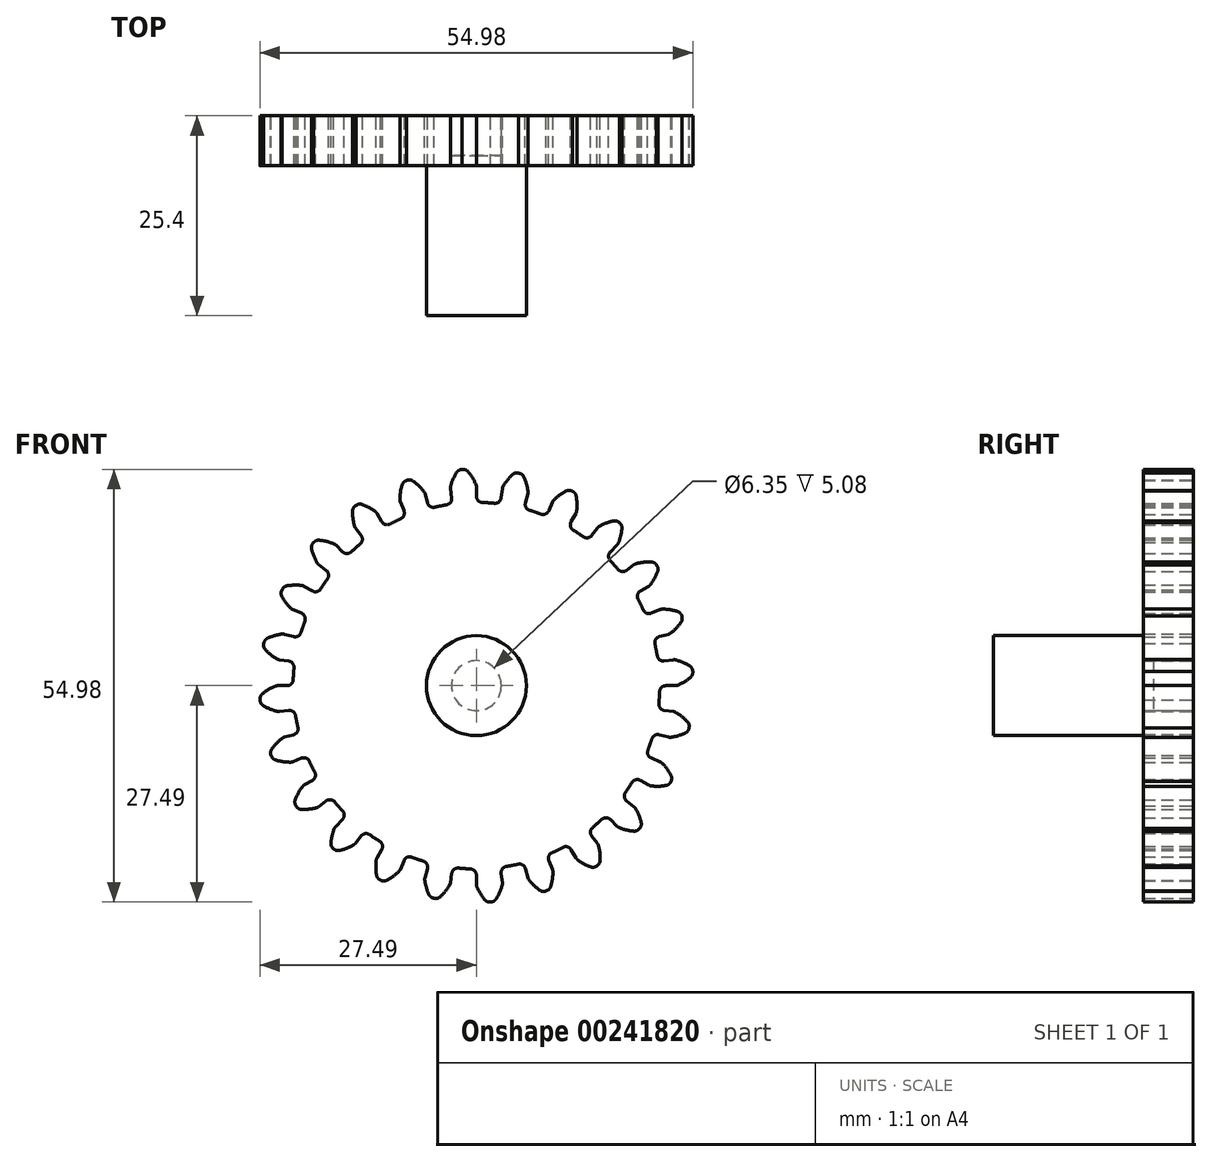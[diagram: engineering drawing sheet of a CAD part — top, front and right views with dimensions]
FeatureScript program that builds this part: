
annotation { "Feature Type Name" : "Feature", "Feature Type Description" : "" }
export const myFeature = defineFeature(function(context is Context, id is Id, definition is map)
    precondition{}
    {
        {
            var Q0;
            Q0=qCreatedBy(makeId("Front.planeOp"),FACE);
            var sketch = newSketch(context, id + "F0", { "sketchPlane" : qUnion([Q0])});
            skArc(sketch, "E0", {"start": v(-3.8, 22.97) * mm, "mid": v(-4.54, 22.84) * mm, "end": v(-5.28, 22.68) * mm});
            skArc(sketch, "E1.trimOffspring", {"start": v(-0.06, 25.55) * mm, "mid": v(-0.5, 26.41) * mm, "end": v(-1.06, 27.2) * mm});
            skLineSegment(sketch, "E2", {"start": v(0, 25.25) * mm, "end": v(0, 24.06) * mm});
            skLineSegment(sketch, "E3", {"start": v(-1.67, 27.49) * mm, "end": v(-1.8, 27.49) * mm});
            skLineSegment(sketch, "E4.MirrorCS", {"start": v(-1.93, 27.47) * mm, "end": v(-1.8, 27.49) * mm});
            skArc(sketch, "E5.MirrorCS", {"start": v(-3.28, 25.34) * mm, "mid": v(-2.95, 26.25) * mm, "end": v(-2.5, 27.1) * mm});
            skLineSegment(sketch, "E6.MirrorCS", {"start": v(-3.3, 25.03) * mm, "end": v(-3.14, 23.86) * mm});
            skPoint(sketch, "E7.visualSharp", {"position": v(-3.04, 23.08) * mm});
            skArc(sketch, "E8.filletArc", {"start": v(-3.8, 22.97) * mm, "mid": v(-3.3, 23.28) * mm, "end": v(-3.14, 23.86) * mm});
            skPoint(sketch, "E9.visualSharp", {"position": v(-3.32, 25.18) * mm});
            skArc(sketch, "E9.filletArc", {"start": v(-3.28, 25.34) * mm, "mid": v(-3.3, 25.19) * mm, "end": v(-3.3, 25.03) * mm});
            skPoint(sketch, "E10.visualSharp", {"position": v(-2.28, 27.42) * mm});
            skArc(sketch, "E10.filletArc", {"start": v(-1.93, 27.47) * mm, "mid": v(-2.25, 27.35) * mm, "end": v(-2.5, 27.1) * mm});
            skPoint(sketch, "E11.visualSharp", {"position": v(0, 25.4) * mm});
            skArc(sketch, "E11.filletArc", {"start": v(0, 25.25) * mm, "mid": v(-0.02, 25.4) * mm, "end": v(-0.06, 25.55) * mm});
            skPoint(sketch, "E12.visualSharp", {"position": v(0, 23.28) * mm});
            skArc(sketch, "E12.filletArc", {"start": v(0, 24.06) * mm, "mid": v(0.22, 23.51) * mm, "end": v(0.77, 23.27) * mm});
            skPoint(sketch, "E13.visualSharp", {"position": v(-1.31, 27.49) * mm});
            skArc(sketch, "E13.filletArc", {"start": v(-1.06, 27.2) * mm, "mid": v(-1.33, 27.41) * mm, "end": v(-1.67, 27.49) * mm});
            skArc(sketch, "E14.1.0", {"start": v(-9.61, 21.2) * mm, "mid": v(-9.2, 21.64) * mm, "end": v(-9.2, 22.23) * mm});
            skLineSegment(sketch, "E14.1.1", {"start": v(-9.66, 23.33) * mm, "end": v(-9.2, 22.23) * mm});
            skArc(sketch, "E14.1.2", {"start": v(-9.72, 23.63) * mm, "mid": v(-9.7, 23.47) * mm, "end": v(-9.66, 23.33) * mm});
            skArc(sketch, "E14.1.3", {"start": v(-9.72, 23.63) * mm, "mid": v(-9.65, 24.6) * mm, "end": v(-9.43, 25.54) * mm});
            skArc(sketch, "E14.1.4", {"start": v(-8.98, 26.03) * mm, "mid": v(-9.26, 25.83) * mm, "end": v(-9.43, 25.54) * mm});
            skLineSegment(sketch, "E14.1.5", {"start": v(-8.98, 26.03) * mm, "end": v(-8.85, 26.08) * mm});
            skLineSegment(sketch, "E14.1.6", {"start": v(-8.73, 26.12) * mm, "end": v(-8.85, 26.08) * mm});
            skArc(sketch, "E14.1.7", {"start": v(-8.07, 26) * mm, "mid": v(-8.38, 26.13) * mm, "end": v(-8.73, 26.12) * mm});
            skArc(sketch, "E14.1.8", {"start": v(-6.67, 24.67) * mm, "mid": v(-7.32, 25.39) * mm, "end": v(-8.07, 26) * mm});
            skArc(sketch, "E14.1.9", {"start": v(-6.53, 24.39) * mm, "mid": v(-6.59, 24.53) * mm, "end": v(-6.67, 24.67) * mm});
            skLineSegment(sketch, "E14.1.10", {"start": v(-6.53, 24.39) * mm, "end": v(-6.23, 23.24) * mm});
            skArc(sketch, "E14.1.11", {"start": v(-6.23, 23.24) * mm, "mid": v(-5.87, 22.77) * mm, "end": v(-5.28, 22.68) * mm});
            skArc(sketch, "E14.2.0", {"start": v(-14.78, 18) * mm, "mid": v(-14.5, 18.52) * mm, "end": v(-14.65, 19.1) * mm});
            skLineSegment(sketch, "E14.2.1", {"start": v(-15.37, 20.03) * mm, "end": v(-14.65, 19.1) * mm});
            skArc(sketch, "E14.2.2", {"start": v(-15.5, 20.3) * mm, "mid": v(-15.45, 20.16) * mm, "end": v(-15.37, 20.03) * mm});
            skArc(sketch, "E14.2.3", {"start": v(-15.5, 20.3) * mm, "mid": v(-15.69, 21.26) * mm, "end": v(-15.72, 22.23) * mm});
            skArc(sketch, "E14.2.4", {"start": v(-15.4, 22.82) * mm, "mid": v(-15.63, 22.56) * mm, "end": v(-15.72, 22.23) * mm});
            skLineSegment(sketch, "E14.2.5", {"start": v(-15.4, 22.82) * mm, "end": v(-15.3, 22.9) * mm});
            skLineSegment(sketch, "E14.2.6", {"start": v(-15.19, 22.97) * mm, "end": v(-15.3, 22.9) * mm});
            skArc(sketch, "E14.2.7", {"start": v(-14.52, 23.03) * mm, "mid": v(-14.86, 23.07) * mm, "end": v(-15.19, 22.97) * mm});
            skArc(sketch, "E14.2.8", {"start": v(-12.83, 22.1) * mm, "mid": v(-13.64, 22.63) * mm, "end": v(-14.52, 23.03) * mm});
            skArc(sketch, "E14.2.9", {"start": v(-12.62, 21.87) * mm, "mid": v(-12.71, 22) * mm, "end": v(-12.83, 22.1) * mm});
            skLineSegment(sketch, "E14.2.10", {"start": v(-12.62, 21.87) * mm, "end": v(-12.03, 20.84) * mm});
            skArc(sketch, "E14.2.11", {"start": v(-12.03, 20.84) * mm, "mid": v(-11.56, 20.47) * mm, "end": v(-10.97, 20.54) * mm});
            skArc(sketch, "E15.2.3.0", {"start": v(-18.93, 13.56) * mm, "mid": v(-18.79, 14.14) * mm, "end": v(-19.1, 14.65) * mm});
            skLineSegment(sketch, "E15.4.3.0", {"start": v(-20.03, 15.37) * mm, "end": v(-19.1, 14.65) * mm});
            skArc(sketch, "E15.7.3.0", {"start": v(-20.23, 15.6) * mm, "mid": v(-20.14, 15.48) * mm, "end": v(-20.03, 15.37) * mm});
            skArc(sketch, "E15.11.3.0", {"start": v(-20.23, 15.6) * mm, "mid": v(-20.65, 16.48) * mm, "end": v(-20.93, 17.4) * mm});
            skArc(sketch, "E15.15.3.0", {"start": v(-20.79, 18.06) * mm, "mid": v(-20.93, 17.75) * mm, "end": v(-20.93, 17.4) * mm});
            skLineSegment(sketch, "E15.19.3.0", {"start": v(-20.79, 18.06) * mm, "end": v(-20.7, 18.16) * mm});
            skLineSegment(sketch, "E15.22.3.0", {"start": v(-20.62, 18.25) * mm, "end": v(-20.7, 18.16) * mm});
            skArc(sketch, "E15.25.3.0", {"start": v(-19.99, 18.48) * mm, "mid": v(-20.33, 18.44) * mm, "end": v(-20.62, 18.25) * mm});
            skArc(sketch, "E15.29.3.0", {"start": v(-18.11, 18.02) * mm, "mid": v(-19.03, 18.33) * mm, "end": v(-19.99, 18.48) * mm});
            skArc(sketch, "E15.33.3.0", {"start": v(-17.85, 17.85) * mm, "mid": v(-17.97, 17.95) * mm, "end": v(-18.11, 18.02) * mm});
            skLineSegment(sketch, "E15.37.3.0", {"start": v(-17.85, 17.85) * mm, "end": v(-17.02, 17.02) * mm});
            skArc(sketch, "E15.40.3.0", {"start": v(-17.02, 17.02) * mm, "mid": v(-16.47, 16.78) * mm, "end": v(-15.91, 17) * mm});
            skArc(sketch, "E15.2.4.0", {"start": v(-21.8, 8.2) * mm, "mid": v(-21.8, 8.8) * mm, "end": v(-22.23, 9.2) * mm});
            skLineSegment(sketch, "E15.4.4.0", {"start": v(-23.33, 9.66) * mm, "end": v(-22.23, 9.2) * mm});
            skArc(sketch, "E15.7.4.0", {"start": v(-23.58, 9.83) * mm, "mid": v(-23.46, 9.74) * mm, "end": v(-23.33, 9.66) * mm});
            skArc(sketch, "E15.11.4.0", {"start": v(-23.58, 9.83) * mm, "mid": v(-24.21, 10.57) * mm, "end": v(-24.72, 11.4) * mm});
            skArc(sketch, "E15.15.4.0", {"start": v(-24.75, 12.06) * mm, "mid": v(-24.81, 11.72) * mm, "end": v(-24.72, 11.4) * mm});
            skLineSegment(sketch, "E15.19.4.0", {"start": v(-24.75, 12.06) * mm, "end": v(-24.7, 12.18) * mm});
            skLineSegment(sketch, "E15.22.4.0", {"start": v(-24.64, 12.3) * mm, "end": v(-24.7, 12.18) * mm});
            skArc(sketch, "E15.25.4.0", {"start": v(-24.09, 12.68) * mm, "mid": v(-24.4, 12.55) * mm, "end": v(-24.64, 12.3) * mm});
            skArc(sketch, "E15.29.4.0", {"start": v(-22.16, 12.72) * mm, "mid": v(-23.12, 12.78) * mm, "end": v(-24.09, 12.68) * mm});
            skArc(sketch, "E15.33.4.0", {"start": v(-21.87, 12.62) * mm, "mid": v(-22, 12.69) * mm, "end": v(-22.16, 12.72) * mm});
            skLineSegment(sketch, "E15.37.4.0", {"start": v(-21.87, 12.62) * mm, "end": v(-20.84, 12.03) * mm});
            skArc(sketch, "E15.40.4.0", {"start": v(-20.84, 12.03) * mm, "mid": v(-20.25, 11.95) * mm, "end": v(-19.77, 12.3) * mm});
            skArc(sketch, "E15.2.5.0", {"start": v(-23.17, 2.28) * mm, "mid": v(-23.34, 2.85) * mm, "end": v(-23.86, 3.14) * mm});
            skLineSegment(sketch, "E15.4.5.0", {"start": v(-25.03, 3.3) * mm, "end": v(-23.86, 3.14) * mm});
            skArc(sketch, "E15.7.5.0", {"start": v(-25.32, 3.4) * mm, "mid": v(-25.18, 3.33) * mm, "end": v(-25.03, 3.3) * mm});
            skArc(sketch, "E15.11.5.0", {"start": v(-25.32, 3.4) * mm, "mid": v(-26.12, 3.94) * mm, "end": v(-26.83, 4.6) * mm});
            skArc(sketch, "E15.15.5.0", {"start": v(-27.03, 5.24) * mm, "mid": v(-27, 4.9) * mm, "end": v(-26.83, 4.6) * mm});
            skLineSegment(sketch, "E15.19.5.0", {"start": v(-27.03, 5.24) * mm, "end": v(-27.01, 5.37) * mm});
            skLineSegment(sketch, "E15.22.5.0", {"start": v(-26.98, 5.5) * mm, "end": v(-27.01, 5.37) * mm});
            skArc(sketch, "E15.25.5.0", {"start": v(-26.55, 6.01) * mm, "mid": v(-26.82, 5.8) * mm, "end": v(-26.98, 5.5) * mm});
            skArc(sketch, "E15.29.5.0", {"start": v(-24.7, 6.55) * mm, "mid": v(-25.64, 6.36) * mm, "end": v(-26.55, 6.01) * mm});
            skArc(sketch, "E15.33.5.0", {"start": v(-24.39, 6.53) * mm, "mid": v(-24.54, 6.56) * mm, "end": v(-24.7, 6.55) * mm});
            skLineSegment(sketch, "E15.37.5.0", {"start": v(-24.39, 6.53) * mm, "end": v(-23.24, 6.23) * mm});
            skArc(sketch, "E15.40.5.0", {"start": v(-23.24, 6.23) * mm, "mid": v(-22.65, 6.3) * mm, "end": v(-22.28, 6.76) * mm});
            skArc(sketch, "E15.2.6.0", {"start": v(-22.97, -3.8) * mm, "mid": v(-23.28, -3.3) * mm, "end": v(-23.86, -3.14) * mm});
            skLineSegment(sketch, "E15.4.6.0", {"start": v(-25.03, -3.3) * mm, "end": v(-23.86, -3.14) * mm});
            skArc(sketch, "E15.7.6.0", {"start": v(-25.34, -3.28) * mm, "mid": v(-25.19, -3.3) * mm, "end": v(-25.03, -3.3) * mm});
            skArc(sketch, "E15.11.6.0", {"start": v(-25.34, -3.28) * mm, "mid": v(-26.25, -2.95) * mm, "end": v(-27.1, -2.5) * mm});
            skArc(sketch, "E15.15.6.0", {"start": v(-27.47, -1.93) * mm, "mid": v(-27.35, -2.25) * mm, "end": v(-27.1, -2.5) * mm});
            skLineSegment(sketch, "E15.19.6.0", {"start": v(-27.47, -1.93) * mm, "end": v(-27.49, -1.8) * mm});
            skLineSegment(sketch, "E15.22.6.0", {"start": v(-27.49, -1.67) * mm, "end": v(-27.49, -1.8) * mm});
            skArc(sketch, "E15.25.6.0", {"start": v(-27.2, -1.06) * mm, "mid": v(-27.41, -1.33) * mm, "end": v(-27.49, -1.67) * mm});
            skArc(sketch, "E15.29.6.0", {"start": v(-25.55, -0.06) * mm, "mid": v(-26.41, -0.5) * mm, "end": v(-27.2, -1.06) * mm});
            skArc(sketch, "E15.33.6.0", {"start": v(-25.25, 0) * mm, "mid": v(-25.4, -0.02) * mm, "end": v(-25.55, -0.06) * mm});
            skLineSegment(sketch, "E15.37.6.0", {"start": v(-25.25, 0) * mm, "end": v(-24.06, 0) * mm});
            skArc(sketch, "E15.40.6.0", {"start": v(-24.06, 0) * mm, "mid": v(-23.51, 0.22) * mm, "end": v(-23.27, 0.77) * mm});
            skArc(sketch, "E15.2.7.0", {"start": v(-21.2, -9.61) * mm, "mid": v(-21.64, -9.2) * mm, "end": v(-22.23, -9.2) * mm});
            skLineSegment(sketch, "E15.4.7.0", {"start": v(-23.33, -9.66) * mm, "end": v(-22.23, -9.2) * mm});
            skArc(sketch, "E15.7.7.0", {"start": v(-23.63, -9.72) * mm, "mid": v(-23.47, -9.7) * mm, "end": v(-23.33, -9.66) * mm});
            skArc(sketch, "E15.11.7.0", {"start": v(-23.63, -9.72) * mm, "mid": v(-24.6, -9.65) * mm, "end": v(-25.54, -9.43) * mm});
            skArc(sketch, "E15.15.7.0", {"start": v(-26.03, -8.98) * mm, "mid": v(-25.83, -9.26) * mm, "end": v(-25.54, -9.43) * mm});
            skLineSegment(sketch, "E15.19.7.0", {"start": v(-26.03, -8.98) * mm, "end": v(-26.08, -8.85) * mm});
            skLineSegment(sketch, "E15.22.7.0", {"start": v(-26.12, -8.73) * mm, "end": v(-26.08, -8.85) * mm});
            skArc(sketch, "E15.25.7.0", {"start": v(-26, -8.07) * mm, "mid": v(-26.13, -8.38) * mm, "end": v(-26.12, -8.73) * mm});
            skArc(sketch, "E15.29.7.0", {"start": v(-24.67, -6.67) * mm, "mid": v(-25.39, -7.32) * mm, "end": v(-26, -8.07) * mm});
            skArc(sketch, "E15.33.7.0", {"start": v(-24.39, -6.53) * mm, "mid": v(-24.53, -6.59) * mm, "end": v(-24.67, -6.67) * mm});
            skLineSegment(sketch, "E15.37.7.0", {"start": v(-24.39, -6.53) * mm, "end": v(-23.24, -6.23) * mm});
            skArc(sketch, "E15.40.7.0", {"start": v(-23.24, -6.23) * mm, "mid": v(-22.77, -5.87) * mm, "end": v(-22.68, -5.28) * mm});
            skArc(sketch, "E15.2.8.0", {"start": v(-18, -14.78) * mm, "mid": v(-18.52, -14.5) * mm, "end": v(-19.1, -14.65) * mm});
            skLineSegment(sketch, "E15.4.8.0", {"start": v(-20.03, -15.37) * mm, "end": v(-19.1, -14.65) * mm});
            skArc(sketch, "E15.7.8.0", {"start": v(-20.3, -15.5) * mm, "mid": v(-20.16, -15.45) * mm, "end": v(-20.03, -15.37) * mm});
            skArc(sketch, "E15.11.8.0", {"start": v(-20.3, -15.5) * mm, "mid": v(-21.26, -15.69) * mm, "end": v(-22.23, -15.72) * mm});
            skArc(sketch, "E15.15.8.0", {"start": v(-22.82, -15.4) * mm, "mid": v(-22.56, -15.63) * mm, "end": v(-22.23, -15.72) * mm});
            skLineSegment(sketch, "E15.19.8.0", {"start": v(-22.82, -15.4) * mm, "end": v(-22.9, -15.3) * mm});
            skLineSegment(sketch, "E15.22.8.0", {"start": v(-22.97, -15.19) * mm, "end": v(-22.9, -15.3) * mm});
            skArc(sketch, "E15.25.8.0", {"start": v(-23.03, -14.52) * mm, "mid": v(-23.07, -14.86) * mm, "end": v(-22.97, -15.19) * mm});
            skArc(sketch, "E15.29.8.0", {"start": v(-22.1, -12.83) * mm, "mid": v(-22.63, -13.64) * mm, "end": v(-23.03, -14.52) * mm});
            skArc(sketch, "E15.33.8.0", {"start": v(-21.87, -12.62) * mm, "mid": v(-22, -12.71) * mm, "end": v(-22.1, -12.83) * mm});
            skLineSegment(sketch, "E15.37.8.0", {"start": v(-21.87, -12.62) * mm, "end": v(-20.84, -12.03) * mm});
            skArc(sketch, "E15.40.8.0", {"start": v(-20.84, -12.03) * mm, "mid": v(-20.47, -11.56) * mm, "end": v(-20.54, -10.97) * mm});
            skArc(sketch, "E15.2.9.0", {"start": v(-13.56, -18.93) * mm, "mid": v(-14.14, -18.79) * mm, "end": v(-14.65, -19.1) * mm});
            skLineSegment(sketch, "E15.4.9.0", {"start": v(-15.37, -20.03) * mm, "end": v(-14.65, -19.1) * mm});
            skArc(sketch, "E15.7.9.0", {"start": v(-15.6, -20.23) * mm, "mid": v(-15.48, -20.14) * mm, "end": v(-15.37, -20.03) * mm});
            skArc(sketch, "E15.11.9.0", {"start": v(-15.6, -20.23) * mm, "mid": v(-16.48, -20.65) * mm, "end": v(-17.4, -20.93) * mm});
            skArc(sketch, "E15.15.9.0", {"start": v(-18.06, -20.79) * mm, "mid": v(-17.75, -20.93) * mm, "end": v(-17.4, -20.93) * mm});
            skLineSegment(sketch, "E15.19.9.0", {"start": v(-18.06, -20.79) * mm, "end": v(-18.16, -20.7) * mm});
            skLineSegment(sketch, "E15.22.9.0", {"start": v(-18.25, -20.62) * mm, "end": v(-18.16, -20.7) * mm});
            skArc(sketch, "E15.25.9.0", {"start": v(-18.48, -19.99) * mm, "mid": v(-18.44, -20.33) * mm, "end": v(-18.25, -20.62) * mm});
            skArc(sketch, "E15.29.9.0", {"start": v(-18.02, -18.11) * mm, "mid": v(-18.33, -19.03) * mm, "end": v(-18.48, -19.99) * mm});
            skArc(sketch, "E15.33.9.0", {"start": v(-17.85, -17.85) * mm, "mid": v(-17.95, -17.97) * mm, "end": v(-18.02, -18.11) * mm});
            skLineSegment(sketch, "E15.37.9.0", {"start": v(-17.85, -17.85) * mm, "end": v(-17.02, -17.02) * mm});
            skArc(sketch, "E15.40.9.0", {"start": v(-17.02, -17.02) * mm, "mid": v(-16.78, -16.47) * mm, "end": v(-17, -15.91) * mm});
            skArc(sketch, "E15.2.10.0", {"start": v(-8.2, -21.8) * mm, "mid": v(-8.8, -21.8) * mm, "end": v(-9.2, -22.23) * mm});
            skLineSegment(sketch, "E15.4.10.0", {"start": v(-9.66, -23.33) * mm, "end": v(-9.2, -22.23) * mm});
            skArc(sketch, "E15.7.10.0", {"start": v(-9.83, -23.58) * mm, "mid": v(-9.74, -23.46) * mm, "end": v(-9.66, -23.33) * mm});
            skArc(sketch, "E15.11.10.0", {"start": v(-9.83, -23.58) * mm, "mid": v(-10.57, -24.21) * mm, "end": v(-11.4, -24.72) * mm});
            skArc(sketch, "E15.15.10.0", {"start": v(-12.06, -24.75) * mm, "mid": v(-11.72, -24.81) * mm, "end": v(-11.4, -24.72) * mm});
            skLineSegment(sketch, "E15.19.10.0", {"start": v(-12.06, -24.75) * mm, "end": v(-12.18, -24.7) * mm});
            skLineSegment(sketch, "E15.22.10.0", {"start": v(-12.3, -24.64) * mm, "end": v(-12.18, -24.7) * mm});
            skArc(sketch, "E15.25.10.0", {"start": v(-12.68, -24.09) * mm, "mid": v(-12.55, -24.4) * mm, "end": v(-12.3, -24.64) * mm});
            skArc(sketch, "E15.29.10.0", {"start": v(-12.72, -22.16) * mm, "mid": v(-12.78, -23.12) * mm, "end": v(-12.68, -24.09) * mm});
            skArc(sketch, "E15.33.10.0", {"start": v(-12.62, -21.87) * mm, "mid": v(-12.69, -22) * mm, "end": v(-12.72, -22.16) * mm});
            skLineSegment(sketch, "E15.37.10.0", {"start": v(-12.62, -21.87) * mm, "end": v(-12.03, -20.84) * mm});
            skArc(sketch, "E15.40.10.0", {"start": v(-12.03, -20.84) * mm, "mid": v(-11.95, -20.25) * mm, "end": v(-12.3, -19.77) * mm});
            skArc(sketch, "E15.2.11.0", {"start": v(-2.28, -23.17) * mm, "mid": v(-2.85, -23.34) * mm, "end": v(-3.14, -23.86) * mm});
            skLineSegment(sketch, "E15.4.11.0", {"start": v(-3.3, -25.03) * mm, "end": v(-3.14, -23.86) * mm});
            skArc(sketch, "E15.7.11.0", {"start": v(-3.4, -25.32) * mm, "mid": v(-3.33, -25.18) * mm, "end": v(-3.3, -25.03) * mm});
            skArc(sketch, "E15.11.11.0", {"start": v(-3.4, -25.32) * mm, "mid": v(-3.94, -26.12) * mm, "end": v(-4.6, -26.83) * mm});
            skArc(sketch, "E15.15.11.0", {"start": v(-5.24, -27.03) * mm, "mid": v(-4.9, -27) * mm, "end": v(-4.6, -26.83) * mm});
            skLineSegment(sketch, "E15.19.11.0", {"start": v(-5.24, -27.03) * mm, "end": v(-5.37, -27.01) * mm});
            skLineSegment(sketch, "E15.22.11.0", {"start": v(-5.5, -26.98) * mm, "end": v(-5.37, -27.01) * mm});
            skArc(sketch, "E15.25.11.0", {"start": v(-6.01, -26.55) * mm, "mid": v(-5.8, -26.82) * mm, "end": v(-5.5, -26.98) * mm});
            skArc(sketch, "E15.29.11.0", {"start": v(-6.55, -24.7) * mm, "mid": v(-6.36, -25.64) * mm, "end": v(-6.01, -26.55) * mm});
            skArc(sketch, "E15.33.11.0", {"start": v(-6.53, -24.39) * mm, "mid": v(-6.56, -24.54) * mm, "end": v(-6.55, -24.7) * mm});
            skLineSegment(sketch, "E15.37.11.0", {"start": v(-6.53, -24.39) * mm, "end": v(-6.23, -23.24) * mm});
            skArc(sketch, "E15.40.11.0", {"start": v(-6.23, -23.24) * mm, "mid": v(-6.3, -22.65) * mm, "end": v(-6.76, -22.28) * mm});
            skArc(sketch, "E15.2.12.0", {"start": v(3.8, -22.97) * mm, "mid": v(3.3, -23.28) * mm, "end": v(3.14, -23.86) * mm});
            skLineSegment(sketch, "E15.4.12.0", {"start": v(3.3, -25.03) * mm, "end": v(3.14, -23.86) * mm});
            skArc(sketch, "E15.7.12.0", {"start": v(3.28, -25.34) * mm, "mid": v(3.3, -25.19) * mm, "end": v(3.3, -25.03) * mm});
            skArc(sketch, "E15.11.12.0", {"start": v(3.28, -25.34) * mm, "mid": v(2.95, -26.25) * mm, "end": v(2.5, -27.1) * mm});
            skArc(sketch, "E15.15.12.0", {"start": v(1.93, -27.47) * mm, "mid": v(2.25, -27.35) * mm, "end": v(2.5, -27.1) * mm});
            skLineSegment(sketch, "E15.19.12.0", {"start": v(1.93, -27.47) * mm, "end": v(1.8, -27.49) * mm});
            skLineSegment(sketch, "E15.22.12.0", {"start": v(1.67, -27.49) * mm, "end": v(1.8, -27.49) * mm});
            skArc(sketch, "E15.25.12.0", {"start": v(1.06, -27.2) * mm, "mid": v(1.33, -27.41) * mm, "end": v(1.67, -27.49) * mm});
            skArc(sketch, "E15.29.12.0", {"start": v(0.06, -25.55) * mm, "mid": v(0.5, -26.41) * mm, "end": v(1.06, -27.2) * mm});
            skArc(sketch, "E15.33.12.0", {"start": v(0, -25.25) * mm, "mid": v(0.02, -25.4) * mm, "end": v(0.06, -25.55) * mm});
            skLineSegment(sketch, "E15.37.12.0", {"start": v(0, -25.25) * mm, "end": v(0, -24.06) * mm});
            skArc(sketch, "E15.40.12.0", {"start": v(0, -24.06) * mm, "mid": v(-0.22, -23.51) * mm, "end": v(-0.77, -23.27) * mm});
            skArc(sketch, "E15.2.13.0", {"start": v(9.61, -21.2) * mm, "mid": v(9.2, -21.64) * mm, "end": v(9.2, -22.23) * mm});
            skLineSegment(sketch, "E15.4.13.0", {"start": v(9.66, -23.33) * mm, "end": v(9.2, -22.23) * mm});
            skArc(sketch, "E15.7.13.0", {"start": v(9.72, -23.63) * mm, "mid": v(9.7, -23.47) * mm, "end": v(9.66, -23.33) * mm});
            skArc(sketch, "E15.11.13.0", {"start": v(9.72, -23.63) * mm, "mid": v(9.65, -24.6) * mm, "end": v(9.43, -25.54) * mm});
            skArc(sketch, "E15.15.13.0", {"start": v(8.98, -26.03) * mm, "mid": v(9.26, -25.83) * mm, "end": v(9.43, -25.54) * mm});
            skLineSegment(sketch, "E15.19.13.0", {"start": v(8.98, -26.03) * mm, "end": v(8.85, -26.08) * mm});
            skLineSegment(sketch, "E15.22.13.0", {"start": v(8.73, -26.12) * mm, "end": v(8.85, -26.08) * mm});
            skArc(sketch, "E15.25.13.0", {"start": v(8.07, -26) * mm, "mid": v(8.38, -26.13) * mm, "end": v(8.73, -26.12) * mm});
            skArc(sketch, "E15.29.13.0", {"start": v(6.67, -24.67) * mm, "mid": v(7.32, -25.39) * mm, "end": v(8.07, -26) * mm});
            skArc(sketch, "E15.33.13.0", {"start": v(6.53, -24.39) * mm, "mid": v(6.59, -24.53) * mm, "end": v(6.67, -24.67) * mm});
            skLineSegment(sketch, "E15.37.13.0", {"start": v(6.53, -24.39) * mm, "end": v(6.23, -23.24) * mm});
            skArc(sketch, "E15.40.13.0", {"start": v(6.23, -23.24) * mm, "mid": v(5.87, -22.77) * mm, "end": v(5.28, -22.68) * mm});
            skArc(sketch, "E15.2.14.0", {"start": v(14.78, -18) * mm, "mid": v(14.5, -18.52) * mm, "end": v(14.65, -19.1) * mm});
            skLineSegment(sketch, "E15.4.14.0", {"start": v(15.37, -20.03) * mm, "end": v(14.65, -19.1) * mm});
            skArc(sketch, "E15.7.14.0", {"start": v(15.5, -20.3) * mm, "mid": v(15.45, -20.16) * mm, "end": v(15.37, -20.03) * mm});
            skArc(sketch, "E15.11.14.0", {"start": v(15.5, -20.3) * mm, "mid": v(15.69, -21.26) * mm, "end": v(15.72, -22.23) * mm});
            skArc(sketch, "E15.15.14.0", {"start": v(15.4, -22.82) * mm, "mid": v(15.63, -22.56) * mm, "end": v(15.72, -22.23) * mm});
            skLineSegment(sketch, "E15.19.14.0", {"start": v(15.4, -22.82) * mm, "end": v(15.3, -22.9) * mm});
            skLineSegment(sketch, "E15.22.14.0", {"start": v(15.19, -22.97) * mm, "end": v(15.3, -22.9) * mm});
            skArc(sketch, "E15.25.14.0", {"start": v(14.52, -23.03) * mm, "mid": v(14.86, -23.07) * mm, "end": v(15.19, -22.97) * mm});
            skArc(sketch, "E15.29.14.0", {"start": v(12.83, -22.1) * mm, "mid": v(13.64, -22.63) * mm, "end": v(14.52, -23.03) * mm});
            skArc(sketch, "E15.33.14.0", {"start": v(12.62, -21.87) * mm, "mid": v(12.71, -22) * mm, "end": v(12.83, -22.1) * mm});
            skLineSegment(sketch, "E15.37.14.0", {"start": v(12.62, -21.87) * mm, "end": v(12.03, -20.84) * mm});
            skArc(sketch, "E15.40.14.0", {"start": v(12.03, -20.84) * mm, "mid": v(11.56, -20.47) * mm, "end": v(10.97, -20.54) * mm});
            skArc(sketch, "E15.2.15.0", {"start": v(18.93, -13.56) * mm, "mid": v(18.79, -14.14) * mm, "end": v(19.1, -14.65) * mm});
            skLineSegment(sketch, "E15.4.15.0", {"start": v(20.03, -15.37) * mm, "end": v(19.1, -14.65) * mm});
            skArc(sketch, "E15.7.15.0", {"start": v(20.23, -15.6) * mm, "mid": v(20.14, -15.48) * mm, "end": v(20.03, -15.37) * mm});
            skArc(sketch, "E15.11.15.0", {"start": v(20.23, -15.6) * mm, "mid": v(20.65, -16.48) * mm, "end": v(20.93, -17.4) * mm});
            skArc(sketch, "E15.15.15.0", {"start": v(20.79, -18.06) * mm, "mid": v(20.93, -17.75) * mm, "end": v(20.93, -17.4) * mm});
            skLineSegment(sketch, "E15.19.15.0", {"start": v(20.79, -18.06) * mm, "end": v(20.7, -18.16) * mm});
            skLineSegment(sketch, "E15.22.15.0", {"start": v(20.62, -18.25) * mm, "end": v(20.7, -18.16) * mm});
            skArc(sketch, "E15.25.15.0", {"start": v(19.99, -18.48) * mm, "mid": v(20.33, -18.44) * mm, "end": v(20.62, -18.25) * mm});
            skArc(sketch, "E15.29.15.0", {"start": v(18.11, -18.02) * mm, "mid": v(19.03, -18.33) * mm, "end": v(19.99, -18.48) * mm});
            skArc(sketch, "E15.33.15.0", {"start": v(17.85, -17.85) * mm, "mid": v(17.97, -17.95) * mm, "end": v(18.11, -18.02) * mm});
            skLineSegment(sketch, "E15.37.15.0", {"start": v(17.85, -17.85) * mm, "end": v(17.02, -17.02) * mm});
            skArc(sketch, "E15.40.15.0", {"start": v(17.02, -17.02) * mm, "mid": v(16.47, -16.78) * mm, "end": v(15.91, -17) * mm});
            skArc(sketch, "E15.2.16.0", {"start": v(21.8, -8.2) * mm, "mid": v(21.8, -8.8) * mm, "end": v(22.23, -9.2) * mm});
            skLineSegment(sketch, "E15.4.16.0", {"start": v(23.33, -9.66) * mm, "end": v(22.23, -9.2) * mm});
            skArc(sketch, "E15.7.16.0", {"start": v(23.58, -9.83) * mm, "mid": v(23.46, -9.74) * mm, "end": v(23.33, -9.66) * mm});
            skArc(sketch, "E15.11.16.0", {"start": v(23.58, -9.83) * mm, "mid": v(24.21, -10.57) * mm, "end": v(24.72, -11.4) * mm});
            skArc(sketch, "E15.15.16.0", {"start": v(24.75, -12.06) * mm, "mid": v(24.81, -11.72) * mm, "end": v(24.72, -11.4) * mm});
            skLineSegment(sketch, "E15.19.16.0", {"start": v(24.75, -12.06) * mm, "end": v(24.7, -12.18) * mm});
            skLineSegment(sketch, "E15.22.16.0", {"start": v(24.64, -12.3) * mm, "end": v(24.7, -12.18) * mm});
            skArc(sketch, "E15.25.16.0", {"start": v(24.09, -12.68) * mm, "mid": v(24.4, -12.55) * mm, "end": v(24.64, -12.3) * mm});
            skArc(sketch, "E15.29.16.0", {"start": v(22.16, -12.72) * mm, "mid": v(23.12, -12.78) * mm, "end": v(24.09, -12.68) * mm});
            skArc(sketch, "E15.33.16.0", {"start": v(21.87, -12.62) * mm, "mid": v(22, -12.69) * mm, "end": v(22.16, -12.72) * mm});
            skLineSegment(sketch, "E15.37.16.0", {"start": v(21.87, -12.62) * mm, "end": v(20.84, -12.03) * mm});
            skArc(sketch, "E15.40.16.0", {"start": v(20.84, -12.03) * mm, "mid": v(20.25, -11.95) * mm, "end": v(19.77, -12.3) * mm});
            skArc(sketch, "E15.2.17.0", {"start": v(23.17, -2.28) * mm, "mid": v(23.34, -2.85) * mm, "end": v(23.86, -3.14) * mm});
            skLineSegment(sketch, "E15.4.17.0", {"start": v(25.03, -3.3) * mm, "end": v(23.86, -3.14) * mm});
            skArc(sketch, "E15.7.17.0", {"start": v(25.32, -3.4) * mm, "mid": v(25.18, -3.33) * mm, "end": v(25.03, -3.3) * mm});
            skArc(sketch, "E15.11.17.0", {"start": v(25.32, -3.4) * mm, "mid": v(26.12, -3.94) * mm, "end": v(26.83, -4.6) * mm});
            skArc(sketch, "E15.15.17.0", {"start": v(27.03, -5.24) * mm, "mid": v(27, -4.9) * mm, "end": v(26.83, -4.6) * mm});
            skLineSegment(sketch, "E15.19.17.0", {"start": v(27.03, -5.24) * mm, "end": v(27.01, -5.37) * mm});
            skLineSegment(sketch, "E15.22.17.0", {"start": v(26.98, -5.5) * mm, "end": v(27.01, -5.37) * mm});
            skArc(sketch, "E15.25.17.0", {"start": v(26.55, -6.01) * mm, "mid": v(26.82, -5.8) * mm, "end": v(26.98, -5.5) * mm});
            skArc(sketch, "E15.29.17.0", {"start": v(24.7, -6.55) * mm, "mid": v(25.64, -6.36) * mm, "end": v(26.55, -6.01) * mm});
            skArc(sketch, "E15.33.17.0", {"start": v(24.39, -6.53) * mm, "mid": v(24.54, -6.56) * mm, "end": v(24.7, -6.55) * mm});
            skLineSegment(sketch, "E15.37.17.0", {"start": v(24.39, -6.53) * mm, "end": v(23.24, -6.23) * mm});
            skArc(sketch, "E15.40.17.0", {"start": v(23.24, -6.23) * mm, "mid": v(22.65, -6.3) * mm, "end": v(22.28, -6.76) * mm});
            skArc(sketch, "E15.2.18.0", {"start": v(22.97, 3.8) * mm, "mid": v(23.28, 3.3) * mm, "end": v(23.86, 3.14) * mm});
            skLineSegment(sketch, "E15.4.18.0", {"start": v(25.03, 3.3) * mm, "end": v(23.86, 3.14) * mm});
            skArc(sketch, "E15.7.18.0", {"start": v(25.34, 3.28) * mm, "mid": v(25.19, 3.3) * mm, "end": v(25.03, 3.3) * mm});
            skArc(sketch, "E15.11.18.0", {"start": v(25.34, 3.28) * mm, "mid": v(26.25, 2.95) * mm, "end": v(27.1, 2.5) * mm});
            skArc(sketch, "E15.15.18.0", {"start": v(27.47, 1.93) * mm, "mid": v(27.35, 2.25) * mm, "end": v(27.1, 2.5) * mm});
            skLineSegment(sketch, "E15.19.18.0", {"start": v(27.47, 1.93) * mm, "end": v(27.49, 1.8) * mm});
            skLineSegment(sketch, "E15.22.18.0", {"start": v(27.49, 1.67) * mm, "end": v(27.49, 1.8) * mm});
            skArc(sketch, "E15.25.18.0", {"start": v(27.2, 1.06) * mm, "mid": v(27.41, 1.33) * mm, "end": v(27.49, 1.67) * mm});
            skArc(sketch, "E15.29.18.0", {"start": v(25.55, 0.06) * mm, "mid": v(26.41, 0.5) * mm, "end": v(27.2, 1.06) * mm});
            skArc(sketch, "E15.33.18.0", {"start": v(25.25, 0) * mm, "mid": v(25.4, 0.02) * mm, "end": v(25.55, 0.06) * mm});
            skLineSegment(sketch, "E15.37.18.0", {"start": v(25.25, 0) * mm, "end": v(24.06, 0) * mm});
            skArc(sketch, "E15.40.18.0", {"start": v(24.06, 0) * mm, "mid": v(23.51, -0.22) * mm, "end": v(23.27, -0.77) * mm});
            skArc(sketch, "E15.2.19.0", {"start": v(21.2, 9.61) * mm, "mid": v(21.64, 9.2) * mm, "end": v(22.23, 9.2) * mm});
            skLineSegment(sketch, "E15.4.19.0", {"start": v(23.33, 9.66) * mm, "end": v(22.23, 9.2) * mm});
            skArc(sketch, "E15.7.19.0", {"start": v(23.63, 9.72) * mm, "mid": v(23.47, 9.7) * mm, "end": v(23.33, 9.66) * mm});
            skArc(sketch, "E15.11.19.0", {"start": v(23.63, 9.72) * mm, "mid": v(24.6, 9.65) * mm, "end": v(25.54, 9.43) * mm});
            skArc(sketch, "E15.15.19.0", {"start": v(26.03, 8.98) * mm, "mid": v(25.83, 9.26) * mm, "end": v(25.54, 9.43) * mm});
            skLineSegment(sketch, "E15.19.19.0", {"start": v(26.03, 8.98) * mm, "end": v(26.08, 8.85) * mm});
            skLineSegment(sketch, "E15.22.19.0", {"start": v(26.12, 8.73) * mm, "end": v(26.08, 8.85) * mm});
            skArc(sketch, "E15.25.19.0", {"start": v(26, 8.07) * mm, "mid": v(26.13, 8.38) * mm, "end": v(26.12, 8.73) * mm});
            skArc(sketch, "E15.29.19.0", {"start": v(24.67, 6.67) * mm, "mid": v(25.39, 7.32) * mm, "end": v(26, 8.07) * mm});
            skArc(sketch, "E15.33.19.0", {"start": v(24.39, 6.53) * mm, "mid": v(24.53, 6.59) * mm, "end": v(24.67, 6.67) * mm});
            skLineSegment(sketch, "E15.37.19.0", {"start": v(24.39, 6.53) * mm, "end": v(23.24, 6.23) * mm});
            skArc(sketch, "E15.40.19.0", {"start": v(23.24, 6.23) * mm, "mid": v(22.77, 5.87) * mm, "end": v(22.68, 5.28) * mm});
            skArc(sketch, "E15.2.20.0", {"start": v(18, 14.78) * mm, "mid": v(18.52, 14.5) * mm, "end": v(19.1, 14.65) * mm});
            skLineSegment(sketch, "E15.4.20.0", {"start": v(20.03, 15.37) * mm, "end": v(19.1, 14.65) * mm});
            skArc(sketch, "E15.7.20.0", {"start": v(20.3, 15.5) * mm, "mid": v(20.16, 15.45) * mm, "end": v(20.03, 15.37) * mm});
            skArc(sketch, "E15.11.20.0", {"start": v(20.3, 15.5) * mm, "mid": v(21.26, 15.69) * mm, "end": v(22.23, 15.72) * mm});
            skArc(sketch, "E15.15.20.0", {"start": v(22.82, 15.4) * mm, "mid": v(22.56, 15.63) * mm, "end": v(22.23, 15.72) * mm});
            skLineSegment(sketch, "E15.19.20.0", {"start": v(22.82, 15.4) * mm, "end": v(22.9, 15.3) * mm});
            skLineSegment(sketch, "E15.22.20.0", {"start": v(22.97, 15.19) * mm, "end": v(22.9, 15.3) * mm});
            skArc(sketch, "E15.25.20.0", {"start": v(23.03, 14.52) * mm, "mid": v(23.07, 14.86) * mm, "end": v(22.97, 15.19) * mm});
            skArc(sketch, "E15.29.20.0", {"start": v(22.1, 12.83) * mm, "mid": v(22.63, 13.64) * mm, "end": v(23.03, 14.52) * mm});
            skArc(sketch, "E15.33.20.0", {"start": v(21.87, 12.62) * mm, "mid": v(22, 12.71) * mm, "end": v(22.1, 12.83) * mm});
            skLineSegment(sketch, "E15.37.20.0", {"start": v(21.87, 12.62) * mm, "end": v(20.84, 12.03) * mm});
            skArc(sketch, "E15.40.20.0", {"start": v(20.84, 12.03) * mm, "mid": v(20.47, 11.56) * mm, "end": v(20.54, 10.97) * mm});
            skArc(sketch, "E15.2.21.0", {"start": v(13.56, 18.93) * mm, "mid": v(14.14, 18.79) * mm, "end": v(14.65, 19.1) * mm});
            skLineSegment(sketch, "E15.4.21.0", {"start": v(15.37, 20.03) * mm, "end": v(14.65, 19.1) * mm});
            skArc(sketch, "E15.7.21.0", {"start": v(15.6, 20.23) * mm, "mid": v(15.48, 20.14) * mm, "end": v(15.37, 20.03) * mm});
            skArc(sketch, "E15.11.21.0", {"start": v(15.6, 20.23) * mm, "mid": v(16.48, 20.65) * mm, "end": v(17.4, 20.93) * mm});
            skArc(sketch, "E15.15.21.0", {"start": v(18.06, 20.79) * mm, "mid": v(17.75, 20.93) * mm, "end": v(17.4, 20.93) * mm});
            skLineSegment(sketch, "E15.19.21.0", {"start": v(18.06, 20.79) * mm, "end": v(18.16, 20.7) * mm});
            skLineSegment(sketch, "E15.22.21.0", {"start": v(18.25, 20.62) * mm, "end": v(18.16, 20.7) * mm});
            skArc(sketch, "E15.25.21.0", {"start": v(18.48, 19.99) * mm, "mid": v(18.44, 20.33) * mm, "end": v(18.25, 20.62) * mm});
            skArc(sketch, "E15.29.21.0", {"start": v(18.02, 18.11) * mm, "mid": v(18.33, 19.03) * mm, "end": v(18.48, 19.99) * mm});
            skArc(sketch, "E15.33.21.0", {"start": v(17.85, 17.85) * mm, "mid": v(17.95, 17.97) * mm, "end": v(18.02, 18.11) * mm});
            skLineSegment(sketch, "E15.37.21.0", {"start": v(17.85, 17.85) * mm, "end": v(17.02, 17.02) * mm});
            skArc(sketch, "E15.40.21.0", {"start": v(17.02, 17.02) * mm, "mid": v(16.78, 16.47) * mm, "end": v(17, 15.91) * mm});
            skArc(sketch, "E15.2.22.0", {"start": v(8.2, 21.8) * mm, "mid": v(8.8, 21.8) * mm, "end": v(9.2, 22.23) * mm});
            skLineSegment(sketch, "E15.4.22.0", {"start": v(9.66, 23.33) * mm, "end": v(9.2, 22.23) * mm});
            skArc(sketch, "E15.7.22.0", {"start": v(9.83, 23.58) * mm, "mid": v(9.74, 23.46) * mm, "end": v(9.66, 23.33) * mm});
            skArc(sketch, "E15.11.22.0", {"start": v(9.83, 23.58) * mm, "mid": v(10.57, 24.21) * mm, "end": v(11.4, 24.72) * mm});
            skArc(sketch, "E15.15.22.0", {"start": v(12.06, 24.75) * mm, "mid": v(11.72, 24.81) * mm, "end": v(11.4, 24.72) * mm});
            skLineSegment(sketch, "E15.19.22.0", {"start": v(12.06, 24.75) * mm, "end": v(12.18, 24.7) * mm});
            skLineSegment(sketch, "E15.22.22.0", {"start": v(12.3, 24.64) * mm, "end": v(12.18, 24.7) * mm});
            skArc(sketch, "E15.25.22.0", {"start": v(12.68, 24.09) * mm, "mid": v(12.55, 24.4) * mm, "end": v(12.3, 24.64) * mm});
            skArc(sketch, "E15.29.22.0", {"start": v(12.72, 22.16) * mm, "mid": v(12.78, 23.12) * mm, "end": v(12.68, 24.09) * mm});
            skArc(sketch, "E15.33.22.0", {"start": v(12.62, 21.87) * mm, "mid": v(12.69, 22) * mm, "end": v(12.72, 22.16) * mm});
            skLineSegment(sketch, "E15.37.22.0", {"start": v(12.62, 21.87) * mm, "end": v(12.03, 20.84) * mm});
            skArc(sketch, "E15.40.22.0", {"start": v(12.03, 20.84) * mm, "mid": v(11.95, 20.25) * mm, "end": v(12.3, 19.77) * mm});
            skArc(sketch, "E15.2.23.0", {"start": v(2.28, 23.17) * mm, "mid": v(2.85, 23.34) * mm, "end": v(3.14, 23.86) * mm});
            skLineSegment(sketch, "E15.4.23.0", {"start": v(3.3, 25.03) * mm, "end": v(3.14, 23.86) * mm});
            skArc(sketch, "E15.7.23.0", {"start": v(3.4, 25.32) * mm, "mid": v(3.33, 25.18) * mm, "end": v(3.3, 25.03) * mm});
            skArc(sketch, "E15.11.23.0", {"start": v(3.4, 25.32) * mm, "mid": v(3.94, 26.12) * mm, "end": v(4.6, 26.83) * mm});
            skArc(sketch, "E15.15.23.0", {"start": v(5.24, 27.03) * mm, "mid": v(4.9, 27) * mm, "end": v(4.6, 26.83) * mm});
            skLineSegment(sketch, "E15.19.23.0", {"start": v(5.24, 27.03) * mm, "end": v(5.37, 27.01) * mm});
            skLineSegment(sketch, "E15.22.23.0", {"start": v(5.5, 26.98) * mm, "end": v(5.37, 27.01) * mm});
            skArc(sketch, "E15.25.23.0", {"start": v(6.01, 26.55) * mm, "mid": v(5.8, 26.82) * mm, "end": v(5.5, 26.98) * mm});
            skArc(sketch, "E15.29.23.0", {"start": v(6.55, 24.7) * mm, "mid": v(6.36, 25.64) * mm, "end": v(6.01, 26.55) * mm});
            skArc(sketch, "E15.33.23.0", {"start": v(6.53, 24.39) * mm, "mid": v(6.56, 24.54) * mm, "end": v(6.55, 24.7) * mm});
            skLineSegment(sketch, "E15.37.23.0", {"start": v(6.53, 24.39) * mm, "end": v(6.23, 23.24) * mm});
            skArc(sketch, "E15.40.23.0", {"start": v(6.23, 23.24) * mm, "mid": v(6.3, 22.65) * mm, "end": v(6.76, 22.28) * mm});
            skArc(sketch, "E16.trimOffspring", {"start": v(2.28, 23.17) * mm, "mid": v(1.52, 23.23) * mm, "end": v(0.77, 23.27) * mm});
            skArc(sketch, "E17.trimOffspring", {"start": v(8.2, 21.8) * mm, "mid": v(7.48, 22.05) * mm, "end": v(6.76, 22.28) * mm});
            skArc(sketch, "E18.trimOffspring", {"start": v(13.56, 18.93) * mm, "mid": v(12.94, 19.36) * mm, "end": v(12.3, 19.77) * mm});
            skArc(sketch, "E19.trimOffspring", {"start": v(18, 14.78) * mm, "mid": v(17.5, 15.35) * mm, "end": v(17, 15.91) * mm});
            skArc(sketch, "E20.trimOffspring", {"start": v(21.2, 9.61) * mm, "mid": v(20.88, 10.3) * mm, "end": v(20.54, 10.97) * mm});
            skArc(sketch, "E21.trimOffspring", {"start": v(22.97, 3.8) * mm, "mid": v(22.84, 4.54) * mm, "end": v(22.68, 5.28) * mm});
            skArc(sketch, "E22.trimOffspring", {"start": v(23.17, -2.28) * mm, "mid": v(23.23, -1.52) * mm, "end": v(23.27, -0.77) * mm});
            skArc(sketch, "E23.trimOffspring", {"start": v(21.8, -8.2) * mm, "mid": v(22.05, -7.48) * mm, "end": v(22.28, -6.76) * mm});
            skArc(sketch, "E24.trimOffspring", {"start": v(18.93, -13.56) * mm, "mid": v(19.36, -12.94) * mm, "end": v(19.77, -12.3) * mm});
            skArc(sketch, "E25.trimOffspring", {"start": v(14.78, -18) * mm, "mid": v(15.35, -17.5) * mm, "end": v(15.91, -17) * mm});
            skArc(sketch, "E26.trimOffspring", {"start": v(9.61, -21.2) * mm, "mid": v(10.3, -20.88) * mm, "end": v(10.97, -20.54) * mm});
            skArc(sketch, "E27.trimOffspring", {"start": v(3.8, -22.97) * mm, "mid": v(4.54, -22.84) * mm, "end": v(5.28, -22.68) * mm});
            skArc(sketch, "E28.trimOffspring", {"start": v(-2.28, -23.17) * mm, "mid": v(-1.52, -23.23) * mm, "end": v(-0.77, -23.27) * mm});
            skArc(sketch, "E29.trimOffspring", {"start": v(-8.2, -21.8) * mm, "mid": v(-7.48, -22.05) * mm, "end": v(-6.76, -22.28) * mm});
            skArc(sketch, "E30.trimOffspring", {"start": v(-13.56, -18.93) * mm, "mid": v(-12.94, -19.36) * mm, "end": v(-12.3, -19.77) * mm});
            skArc(sketch, "E31.trimOffspring", {"start": v(-18, -14.78) * mm, "mid": v(-17.5, -15.35) * mm, "end": v(-17, -15.91) * mm});
            skArc(sketch, "E32.trimOffspring", {"start": v(-21.2, -9.61) * mm, "mid": v(-20.88, -10.3) * mm, "end": v(-20.54, -10.97) * mm});
            skArc(sketch, "E33.trimOffspring", {"start": v(-22.97, -3.8) * mm, "mid": v(-22.84, -4.54) * mm, "end": v(-22.68, -5.28) * mm});
            skArc(sketch, "E34.trimOffspring", {"start": v(-23.17, 2.28) * mm, "mid": v(-23.23, 1.52) * mm, "end": v(-23.27, 0.77) * mm});
            skArc(sketch, "E35.trimOffspring", {"start": v(-21.8, 8.2) * mm, "mid": v(-22.05, 7.48) * mm, "end": v(-22.28, 6.76) * mm});
            skArc(sketch, "E36.trimOffspring", {"start": v(-18.93, 13.56) * mm, "mid": v(-19.36, 12.94) * mm, "end": v(-19.77, 12.3) * mm});
            skArc(sketch, "E37.trimOffspring", {"start": v(-14.78, 18) * mm, "mid": v(-15.35, 17.5) * mm, "end": v(-15.91, 17) * mm});
            skArc(sketch, "E38.trimOffspring", {"start": v(-9.61, 21.2) * mm, "mid": v(-10.3, 20.88) * mm, "end": v(-10.97, 20.54) * mm});
            skSolve(sketch);
        }
        {
            var Q0;
            Q0=qSketchRegion(id+"F0",true);
            var Q1;
            Q1=makeQuery(id+"F0.imprint","IMPRINT",FACE,{"disambiguationData":[TD([[makeQuery(id+"F0.imprint","IMPRINT",EDGE,{"derivedFrom":sQuery(id+"F0.wireOp",EDGE,"E0")}),1.0]])]});
            extrude(context, id + "F1", {"entities" : qUnion([Q0, Q1]), "depth" : 6.35 * mm});
        }
        {
            var Q0;
            Q0=makeQuery(id+"F1.opExtrude","CAP_FACE",FACE,{"disambiguationData":[OSD([sQuery(id+"F0.wireOp",EDGE,"E0"),sQuery(id+"F0.wireOp",EDGE,"E1.trimOffspring"),sQuery(id+"F0.wireOp",EDGE,"E2"),sQuery(id+"F0.wireOp",EDGE,"E3"),sQuery(id+"F0.wireOp",EDGE,"E4.MirrorCS"),sQuery(id+"F0.wireOp",EDGE,"E5.MirrorCS"),sQuery(id+"F0.wireOp",EDGE,"E6.MirrorCS"),sQuery(id+"F0.wireOp",EDGE,"E8.filletArc"),sQuery(id+"F0.wireOp",EDGE,"E9.filletArc"),sQuery(id+"F0.wireOp",EDGE,"E10.filletArc"),sQuery(id+"F0.wireOp",EDGE,"E11.filletArc"),sQuery(id+"F0.wireOp",EDGE,"E12.filletArc"),sQuery(id+"F0.wireOp",EDGE,"E13.filletArc"),sQuery(id+"F0.wireOp",EDGE,"E14.1.0"),sQuery(id+"F0.wireOp",EDGE,"E14.1.1"),sQuery(id+"F0.wireOp",EDGE,"E14.1.2"),sQuery(id+"F0.wireOp",EDGE,"E14.1.3"),sQuery(id+"F0.wireOp",EDGE,"E14.1.4"),sQuery(id+"F0.wireOp",EDGE,"E14.1.5"),sQuery(id+"F0.wireOp",EDGE,"E14.1.6"),sQuery(id+"F0.wireOp",EDGE,"E14.1.7"),sQuery(id+"F0.wireOp",EDGE,"E14.1.8"),sQuery(id+"F0.wireOp",EDGE,"E14.1.9"),sQuery(id+"F0.wireOp",EDGE,"E14.1.10"),sQuery(id+"F0.wireOp",EDGE,"E14.1.11"),sQuery(id+"F0.wireOp",EDGE,"E14.2.0"),sQuery(id+"F0.wireOp",EDGE,"E14.2.1"),sQuery(id+"F0.wireOp",EDGE,"E14.2.2"),sQuery(id+"F0.wireOp",EDGE,"E14.2.3"),sQuery(id+"F0.wireOp",EDGE,"E14.2.4"),sQuery(id+"F0.wireOp",EDGE,"E14.2.5"),sQuery(id+"F0.wireOp",EDGE,"E14.2.6"),sQuery(id+"F0.wireOp",EDGE,"E14.2.7"),sQuery(id+"F0.wireOp",EDGE,"E14.2.8"),sQuery(id+"F0.wireOp",EDGE,"E14.2.9"),sQuery(id+"F0.wireOp",EDGE,"E14.2.10"),sQuery(id+"F0.wireOp",EDGE,"E14.2.11"),sQuery(id+"F0.wireOp",EDGE,"E15.2.3.0"),sQuery(id+"F0.wireOp",EDGE,"E15.4.3.0"),sQuery(id+"F0.wireOp",EDGE,"E15.7.3.0"),sQuery(id+"F0.wireOp",EDGE,"E15.11.3.0"),sQuery(id+"F0.wireOp",EDGE,"E15.15.3.0"),sQuery(id+"F0.wireOp",EDGE,"E15.19.3.0"),sQuery(id+"F0.wireOp",EDGE,"E15.22.3.0"),sQuery(id+"F0.wireOp",EDGE,"E15.25.3.0"),sQuery(id+"F0.wireOp",EDGE,"E15.29.3.0"),sQuery(id+"F0.wireOp",EDGE,"E15.33.3.0"),sQuery(id+"F0.wireOp",EDGE,"E15.37.3.0"),sQuery(id+"F0.wireOp",EDGE,"E15.40.3.0"),sQuery(id+"F0.wireOp",EDGE,"E15.2.4.0"),sQuery(id+"F0.wireOp",EDGE,"E15.4.4.0"),sQuery(id+"F0.wireOp",EDGE,"E15.7.4.0"),sQuery(id+"F0.wireOp",EDGE,"E15.11.4.0"),sQuery(id+"F0.wireOp",EDGE,"E15.15.4.0"),sQuery(id+"F0.wireOp",EDGE,"E15.19.4.0"),sQuery(id+"F0.wireOp",EDGE,"E15.22.4.0"),sQuery(id+"F0.wireOp",EDGE,"E15.25.4.0"),sQuery(id+"F0.wireOp",EDGE,"E15.29.4.0"),sQuery(id+"F0.wireOp",EDGE,"E15.33.4.0"),sQuery(id+"F0.wireOp",EDGE,"E15.37.4.0"),sQuery(id+"F0.wireOp",EDGE,"E15.40.4.0"),sQuery(id+"F0.wireOp",EDGE,"E15.2.5.0"),sQuery(id+"F0.wireOp",EDGE,"E15.4.5.0"),sQuery(id+"F0.wireOp",EDGE,"E15.7.5.0"),sQuery(id+"F0.wireOp",EDGE,"E15.11.5.0"),sQuery(id+"F0.wireOp",EDGE,"E15.15.5.0"),sQuery(id+"F0.wireOp",EDGE,"E15.19.5.0"),sQuery(id+"F0.wireOp",EDGE,"E15.22.5.0"),sQuery(id+"F0.wireOp",EDGE,"E15.25.5.0"),sQuery(id+"F0.wireOp",EDGE,"E15.29.5.0"),sQuery(id+"F0.wireOp",EDGE,"E15.33.5.0"),sQuery(id+"F0.wireOp",EDGE,"E15.37.5.0"),sQuery(id+"F0.wireOp",EDGE,"E15.40.5.0"),sQuery(id+"F0.wireOp",EDGE,"E15.2.6.0"),sQuery(id+"F0.wireOp",EDGE,"E15.4.6.0"),sQuery(id+"F0.wireOp",EDGE,"E15.7.6.0"),sQuery(id+"F0.wireOp",EDGE,"E15.11.6.0"),sQuery(id+"F0.wireOp",EDGE,"E15.15.6.0"),sQuery(id+"F0.wireOp",EDGE,"E15.19.6.0"),sQuery(id+"F0.wireOp",EDGE,"E15.22.6.0"),sQuery(id+"F0.wireOp",EDGE,"E15.25.6.0"),sQuery(id+"F0.wireOp",EDGE,"E15.29.6.0"),sQuery(id+"F0.wireOp",EDGE,"E15.33.6.0"),sQuery(id+"F0.wireOp",EDGE,"E15.37.6.0"),sQuery(id+"F0.wireOp",EDGE,"E15.40.6.0"),sQuery(id+"F0.wireOp",EDGE,"E15.2.7.0"),sQuery(id+"F0.wireOp",EDGE,"E15.4.7.0"),sQuery(id+"F0.wireOp",EDGE,"E15.7.7.0"),sQuery(id+"F0.wireOp",EDGE,"E15.11.7.0"),sQuery(id+"F0.wireOp",EDGE,"E15.15.7.0"),sQuery(id+"F0.wireOp",EDGE,"E15.19.7.0"),sQuery(id+"F0.wireOp",EDGE,"E15.22.7.0"),sQuery(id+"F0.wireOp",EDGE,"E15.25.7.0"),sQuery(id+"F0.wireOp",EDGE,"E15.29.7.0"),sQuery(id+"F0.wireOp",EDGE,"E15.33.7.0"),sQuery(id+"F0.wireOp",EDGE,"E15.37.7.0"),sQuery(id+"F0.wireOp",EDGE,"E15.40.7.0"),sQuery(id+"F0.wireOp",EDGE,"E15.2.8.0"),sQuery(id+"F0.wireOp",EDGE,"E15.4.8.0"),sQuery(id+"F0.wireOp",EDGE,"E15.7.8.0"),sQuery(id+"F0.wireOp",EDGE,"E15.11.8.0"),sQuery(id+"F0.wireOp",EDGE,"E15.15.8.0"),sQuery(id+"F0.wireOp",EDGE,"E15.19.8.0"),sQuery(id+"F0.wireOp",EDGE,"E15.22.8.0"),sQuery(id+"F0.wireOp",EDGE,"E15.25.8.0"),sQuery(id+"F0.wireOp",EDGE,"E15.29.8.0"),sQuery(id+"F0.wireOp",EDGE,"E15.33.8.0"),sQuery(id+"F0.wireOp",EDGE,"E15.37.8.0"),sQuery(id+"F0.wireOp",EDGE,"E15.40.8.0"),sQuery(id+"F0.wireOp",EDGE,"E15.2.9.0"),sQuery(id+"F0.wireOp",EDGE,"E15.4.9.0"),sQuery(id+"F0.wireOp",EDGE,"E15.7.9.0"),sQuery(id+"F0.wireOp",EDGE,"E15.11.9.0"),sQuery(id+"F0.wireOp",EDGE,"E15.15.9.0"),sQuery(id+"F0.wireOp",EDGE,"E15.19.9.0"),sQuery(id+"F0.wireOp",EDGE,"E15.22.9.0"),sQuery(id+"F0.wireOp",EDGE,"E15.25.9.0"),sQuery(id+"F0.wireOp",EDGE,"E15.29.9.0"),sQuery(id+"F0.wireOp",EDGE,"E15.33.9.0"),sQuery(id+"F0.wireOp",EDGE,"E15.37.9.0"),sQuery(id+"F0.wireOp",EDGE,"E15.40.9.0"),sQuery(id+"F0.wireOp",EDGE,"E15.2.10.0"),sQuery(id+"F0.wireOp",EDGE,"E15.4.10.0"),sQuery(id+"F0.wireOp",EDGE,"E15.7.10.0"),sQuery(id+"F0.wireOp",EDGE,"E15.11.10.0"),sQuery(id+"F0.wireOp",EDGE,"E15.15.10.0"),sQuery(id+"F0.wireOp",EDGE,"E15.19.10.0"),sQuery(id+"F0.wireOp",EDGE,"E15.22.10.0"),sQuery(id+"F0.wireOp",EDGE,"E15.25.10.0"),sQuery(id+"F0.wireOp",EDGE,"E15.29.10.0"),sQuery(id+"F0.wireOp",EDGE,"E15.33.10.0"),sQuery(id+"F0.wireOp",EDGE,"E15.37.10.0"),sQuery(id+"F0.wireOp",EDGE,"E15.40.10.0"),sQuery(id+"F0.wireOp",EDGE,"E15.2.11.0"),sQuery(id+"F0.wireOp",EDGE,"E15.4.11.0"),sQuery(id+"F0.wireOp",EDGE,"E15.7.11.0"),sQuery(id+"F0.wireOp",EDGE,"E15.11.11.0"),sQuery(id+"F0.wireOp",EDGE,"E15.15.11.0"),sQuery(id+"F0.wireOp",EDGE,"E15.19.11.0"),sQuery(id+"F0.wireOp",EDGE,"E15.22.11.0"),sQuery(id+"F0.wireOp",EDGE,"E15.25.11.0"),sQuery(id+"F0.wireOp",EDGE,"E15.29.11.0"),sQuery(id+"F0.wireOp",EDGE,"E15.33.11.0"),sQuery(id+"F0.wireOp",EDGE,"E15.37.11.0"),sQuery(id+"F0.wireOp",EDGE,"E15.40.11.0"),sQuery(id+"F0.wireOp",EDGE,"E15.2.12.0"),sQuery(id+"F0.wireOp",EDGE,"E15.4.12.0"),sQuery(id+"F0.wireOp",EDGE,"E15.7.12.0"),sQuery(id+"F0.wireOp",EDGE,"E15.11.12.0"),sQuery(id+"F0.wireOp",EDGE,"E15.15.12.0"),sQuery(id+"F0.wireOp",EDGE,"E15.19.12.0"),sQuery(id+"F0.wireOp",EDGE,"E15.22.12.0"),sQuery(id+"F0.wireOp",EDGE,"E15.25.12.0"),sQuery(id+"F0.wireOp",EDGE,"E15.29.12.0"),sQuery(id+"F0.wireOp",EDGE,"E15.33.12.0"),sQuery(id+"F0.wireOp",EDGE,"E15.37.12.0"),sQuery(id+"F0.wireOp",EDGE,"E15.40.12.0"),sQuery(id+"F0.wireOp",EDGE,"E15.2.13.0"),sQuery(id+"F0.wireOp",EDGE,"E15.4.13.0"),sQuery(id+"F0.wireOp",EDGE,"E15.7.13.0"),sQuery(id+"F0.wireOp",EDGE,"E15.11.13.0"),sQuery(id+"F0.wireOp",EDGE,"E15.15.13.0"),sQuery(id+"F0.wireOp",EDGE,"E15.19.13.0"),sQuery(id+"F0.wireOp",EDGE,"E15.22.13.0"),sQuery(id+"F0.wireOp",EDGE,"E15.25.13.0"),sQuery(id+"F0.wireOp",EDGE,"E15.29.13.0"),sQuery(id+"F0.wireOp",EDGE,"E15.33.13.0"),sQuery(id+"F0.wireOp",EDGE,"E15.37.13.0"),sQuery(id+"F0.wireOp",EDGE,"E15.40.13.0"),sQuery(id+"F0.wireOp",EDGE,"E15.2.14.0"),sQuery(id+"F0.wireOp",EDGE,"E15.4.14.0"),sQuery(id+"F0.wireOp",EDGE,"E15.7.14.0"),sQuery(id+"F0.wireOp",EDGE,"E15.11.14.0"),sQuery(id+"F0.wireOp",EDGE,"E15.15.14.0"),sQuery(id+"F0.wireOp",EDGE,"E15.19.14.0"),sQuery(id+"F0.wireOp",EDGE,"E15.22.14.0"),sQuery(id+"F0.wireOp",EDGE,"E15.25.14.0"),sQuery(id+"F0.wireOp",EDGE,"E15.29.14.0"),sQuery(id+"F0.wireOp",EDGE,"E15.33.14.0"),sQuery(id+"F0.wireOp",EDGE,"E15.37.14.0"),sQuery(id+"F0.wireOp",EDGE,"E15.40.14.0"),sQuery(id+"F0.wireOp",EDGE,"E15.2.15.0"),sQuery(id+"F0.wireOp",EDGE,"E15.4.15.0"),sQuery(id+"F0.wireOp",EDGE,"E15.7.15.0"),sQuery(id+"F0.wireOp",EDGE,"E15.11.15.0"),sQuery(id+"F0.wireOp",EDGE,"E15.15.15.0"),sQuery(id+"F0.wireOp",EDGE,"E15.19.15.0"),sQuery(id+"F0.wireOp",EDGE,"E15.22.15.0"),sQuery(id+"F0.wireOp",EDGE,"E15.25.15.0"),sQuery(id+"F0.wireOp",EDGE,"E15.29.15.0"),sQuery(id+"F0.wireOp",EDGE,"E15.33.15.0"),sQuery(id+"F0.wireOp",EDGE,"E15.37.15.0"),sQuery(id+"F0.wireOp",EDGE,"E15.40.15.0"),sQuery(id+"F0.wireOp",EDGE,"E15.2.16.0"),sQuery(id+"F0.wireOp",EDGE,"E15.4.16.0"),sQuery(id+"F0.wireOp",EDGE,"E15.7.16.0"),sQuery(id+"F0.wireOp",EDGE,"E15.11.16.0"),sQuery(id+"F0.wireOp",EDGE,"E15.15.16.0"),sQuery(id+"F0.wireOp",EDGE,"E15.19.16.0"),sQuery(id+"F0.wireOp",EDGE,"E15.22.16.0"),sQuery(id+"F0.wireOp",EDGE,"E15.25.16.0"),sQuery(id+"F0.wireOp",EDGE,"E15.29.16.0"),sQuery(id+"F0.wireOp",EDGE,"E15.33.16.0"),sQuery(id+"F0.wireOp",EDGE,"E15.37.16.0"),sQuery(id+"F0.wireOp",EDGE,"E15.40.16.0"),sQuery(id+"F0.wireOp",EDGE,"E15.2.17.0"),sQuery(id+"F0.wireOp",EDGE,"E15.4.17.0"),sQuery(id+"F0.wireOp",EDGE,"E15.7.17.0"),sQuery(id+"F0.wireOp",EDGE,"E15.11.17.0"),sQuery(id+"F0.wireOp",EDGE,"E15.15.17.0"),sQuery(id+"F0.wireOp",EDGE,"E15.19.17.0"),sQuery(id+"F0.wireOp",EDGE,"E15.22.17.0"),sQuery(id+"F0.wireOp",EDGE,"E15.25.17.0"),sQuery(id+"F0.wireOp",EDGE,"E15.29.17.0"),sQuery(id+"F0.wireOp",EDGE,"E15.33.17.0"),sQuery(id+"F0.wireOp",EDGE,"E15.37.17.0"),sQuery(id+"F0.wireOp",EDGE,"E15.40.17.0"),sQuery(id+"F0.wireOp",EDGE,"E15.2.18.0"),sQuery(id+"F0.wireOp",EDGE,"E15.4.18.0"),sQuery(id+"F0.wireOp",EDGE,"E15.7.18.0"),sQuery(id+"F0.wireOp",EDGE,"E15.11.18.0"),sQuery(id+"F0.wireOp",EDGE,"E15.15.18.0"),sQuery(id+"F0.wireOp",EDGE,"E15.19.18.0"),sQuery(id+"F0.wireOp",EDGE,"E15.22.18.0"),sQuery(id+"F0.wireOp",EDGE,"E15.25.18.0"),sQuery(id+"F0.wireOp",EDGE,"E15.29.18.0"),sQuery(id+"F0.wireOp",EDGE,"E15.33.18.0"),sQuery(id+"F0.wireOp",EDGE,"E15.37.18.0"),sQuery(id+"F0.wireOp",EDGE,"E15.40.18.0"),sQuery(id+"F0.wireOp",EDGE,"E15.2.19.0"),sQuery(id+"F0.wireOp",EDGE,"E15.4.19.0"),sQuery(id+"F0.wireOp",EDGE,"E15.7.19.0"),sQuery(id+"F0.wireOp",EDGE,"E15.11.19.0"),sQuery(id+"F0.wireOp",EDGE,"E15.15.19.0"),sQuery(id+"F0.wireOp",EDGE,"E15.19.19.0"),sQuery(id+"F0.wireOp",EDGE,"E15.22.19.0"),sQuery(id+"F0.wireOp",EDGE,"E15.25.19.0"),sQuery(id+"F0.wireOp",EDGE,"E15.29.19.0"),sQuery(id+"F0.wireOp",EDGE,"E15.33.19.0"),sQuery(id+"F0.wireOp",EDGE,"E15.37.19.0"),sQuery(id+"F0.wireOp",EDGE,"E15.40.19.0"),sQuery(id+"F0.wireOp",EDGE,"E15.2.20.0"),sQuery(id+"F0.wireOp",EDGE,"E15.4.20.0"),sQuery(id+"F0.wireOp",EDGE,"E15.7.20.0"),sQuery(id+"F0.wireOp",EDGE,"E15.11.20.0"),sQuery(id+"F0.wireOp",EDGE,"E15.15.20.0"),sQuery(id+"F0.wireOp",EDGE,"E15.19.20.0"),sQuery(id+"F0.wireOp",EDGE,"E15.22.20.0"),sQuery(id+"F0.wireOp",EDGE,"E15.25.20.0"),sQuery(id+"F0.wireOp",EDGE,"E15.29.20.0"),sQuery(id+"F0.wireOp",EDGE,"E15.33.20.0"),sQuery(id+"F0.wireOp",EDGE,"E15.37.20.0"),sQuery(id+"F0.wireOp",EDGE,"E15.40.20.0"),sQuery(id+"F0.wireOp",EDGE,"E15.2.21.0"),sQuery(id+"F0.wireOp",EDGE,"E15.4.21.0"),sQuery(id+"F0.wireOp",EDGE,"E15.7.21.0"),sQuery(id+"F0.wireOp",EDGE,"E15.11.21.0"),sQuery(id+"F0.wireOp",EDGE,"E15.15.21.0"),sQuery(id+"F0.wireOp",EDGE,"E15.19.21.0"),sQuery(id+"F0.wireOp",EDGE,"E15.22.21.0"),sQuery(id+"F0.wireOp",EDGE,"E15.25.21.0"),sQuery(id+"F0.wireOp",EDGE,"E15.29.21.0"),sQuery(id+"F0.wireOp",EDGE,"E15.33.21.0"),sQuery(id+"F0.wireOp",EDGE,"E15.37.21.0"),sQuery(id+"F0.wireOp",EDGE,"E15.40.21.0"),sQuery(id+"F0.wireOp",EDGE,"E15.2.22.0"),sQuery(id+"F0.wireOp",EDGE,"E15.4.22.0"),sQuery(id+"F0.wireOp",EDGE,"E15.7.22.0"),sQuery(id+"F0.wireOp",EDGE,"E15.11.22.0"),sQuery(id+"F0.wireOp",EDGE,"E15.15.22.0"),sQuery(id+"F0.wireOp",EDGE,"E15.19.22.0"),sQuery(id+"F0.wireOp",EDGE,"E15.22.22.0"),sQuery(id+"F0.wireOp",EDGE,"E15.25.22.0"),sQuery(id+"F0.wireOp",EDGE,"E15.29.22.0"),sQuery(id+"F0.wireOp",EDGE,"E15.33.22.0"),sQuery(id+"F0.wireOp",EDGE,"E15.37.22.0"),sQuery(id+"F0.wireOp",EDGE,"E15.40.22.0"),sQuery(id+"F0.wireOp",EDGE,"E15.2.23.0"),sQuery(id+"F0.wireOp",EDGE,"E15.4.23.0"),sQuery(id+"F0.wireOp",EDGE,"E15.7.23.0"),sQuery(id+"F0.wireOp",EDGE,"E15.11.23.0"),sQuery(id+"F0.wireOp",EDGE,"E15.15.23.0"),sQuery(id+"F0.wireOp",EDGE,"E15.19.23.0"),sQuery(id+"F0.wireOp",EDGE,"E15.22.23.0"),sQuery(id+"F0.wireOp",EDGE,"E15.25.23.0"),sQuery(id+"F0.wireOp",EDGE,"E15.29.23.0"),sQuery(id+"F0.wireOp",EDGE,"E15.33.23.0"),sQuery(id+"F0.wireOp",EDGE,"E15.37.23.0"),sQuery(id+"F0.wireOp",EDGE,"E15.40.23.0"),sQuery(id+"F0.wireOp",EDGE,"E16.trimOffspring"),sQuery(id+"F0.wireOp",EDGE,"E17.trimOffspring"),sQuery(id+"F0.wireOp",EDGE,"E18.trimOffspring"),sQuery(id+"F0.wireOp",EDGE,"E19.trimOffspring"),sQuery(id+"F0.wireOp",EDGE,"E20.trimOffspring"),sQuery(id+"F0.wireOp",EDGE,"E21.trimOffspring"),sQuery(id+"F0.wireOp",EDGE,"E22.trimOffspring"),sQuery(id+"F0.wireOp",EDGE,"E23.trimOffspring"),sQuery(id+"F0.wireOp",EDGE,"E24.trimOffspring"),sQuery(id+"F0.wireOp",EDGE,"E25.trimOffspring"),sQuery(id+"F0.wireOp",EDGE,"E26.trimOffspring"),sQuery(id+"F0.wireOp",EDGE,"E27.trimOffspring"),sQuery(id+"F0.wireOp",EDGE,"E28.trimOffspring"),sQuery(id+"F0.wireOp",EDGE,"E29.trimOffspring"),sQuery(id+"F0.wireOp",EDGE,"E30.trimOffspring"),sQuery(id+"F0.wireOp",EDGE,"E31.trimOffspring"),sQuery(id+"F0.wireOp",EDGE,"E32.trimOffspring"),sQuery(id+"F0.wireOp",EDGE,"E33.trimOffspring"),sQuery(id+"F0.wireOp",EDGE,"E34.trimOffspring"),sQuery(id+"F0.wireOp",EDGE,"E35.trimOffspring"),sQuery(id+"F0.wireOp",EDGE,"E36.trimOffspring"),sQuery(id+"F0.wireOp",EDGE,"E37.trimOffspring"),sQuery(id+"F0.wireOp",EDGE,"E38.trimOffspring")])],"isStart":false});
            var sketch = newSketch(context, id + "F2", { "sketchPlane" : qUnion([Q0])});
            skCircle(sketch, "E39", {"center": v(0, 0) * mm, "radius": 6.35 * mm});
            skSolve(sketch);
        }
        {
            var Q0;
            Q0 = qSketchRegion(id + "F2", true);
            extrude(context, id + "F3", {"entities" : qUnion([Q0]), "operationType" : NewBodyOperationType.ADD, "depth" : 19.05 * mm});
        }
        {
            var Q0;
            Q0=makeQuery(id+"F1.opExtrude","CAP_FACE",FACE,{"disambiguationData":[OSD([sQuery(id+"F0.wireOp",EDGE,"E0"),sQuery(id+"F0.wireOp",EDGE,"E1.trimOffspring"),sQuery(id+"F0.wireOp",EDGE,"E2"),sQuery(id+"F0.wireOp",EDGE,"E3"),sQuery(id+"F0.wireOp",EDGE,"E4.MirrorCS"),sQuery(id+"F0.wireOp",EDGE,"E5.MirrorCS"),sQuery(id+"F0.wireOp",EDGE,"E6.MirrorCS"),sQuery(id+"F0.wireOp",EDGE,"E8.filletArc"),sQuery(id+"F0.wireOp",EDGE,"E9.filletArc"),sQuery(id+"F0.wireOp",EDGE,"E10.filletArc"),sQuery(id+"F0.wireOp",EDGE,"E11.filletArc"),sQuery(id+"F0.wireOp",EDGE,"E12.filletArc"),sQuery(id+"F0.wireOp",EDGE,"E13.filletArc"),sQuery(id+"F0.wireOp",EDGE,"E14.1.0"),sQuery(id+"F0.wireOp",EDGE,"E14.1.1"),sQuery(id+"F0.wireOp",EDGE,"E14.1.2"),sQuery(id+"F0.wireOp",EDGE,"E14.1.3"),sQuery(id+"F0.wireOp",EDGE,"E14.1.4"),sQuery(id+"F0.wireOp",EDGE,"E14.1.5"),sQuery(id+"F0.wireOp",EDGE,"E14.1.6"),sQuery(id+"F0.wireOp",EDGE,"E14.1.7"),sQuery(id+"F0.wireOp",EDGE,"E14.1.8"),sQuery(id+"F0.wireOp",EDGE,"E14.1.9"),sQuery(id+"F0.wireOp",EDGE,"E14.1.10"),sQuery(id+"F0.wireOp",EDGE,"E14.1.11"),sQuery(id+"F0.wireOp",EDGE,"E14.2.0"),sQuery(id+"F0.wireOp",EDGE,"E14.2.1"),sQuery(id+"F0.wireOp",EDGE,"E14.2.2"),sQuery(id+"F0.wireOp",EDGE,"E14.2.3"),sQuery(id+"F0.wireOp",EDGE,"E14.2.4"),sQuery(id+"F0.wireOp",EDGE,"E14.2.5"),sQuery(id+"F0.wireOp",EDGE,"E14.2.6"),sQuery(id+"F0.wireOp",EDGE,"E14.2.7"),sQuery(id+"F0.wireOp",EDGE,"E14.2.8"),sQuery(id+"F0.wireOp",EDGE,"E14.2.9"),sQuery(id+"F0.wireOp",EDGE,"E14.2.10"),sQuery(id+"F0.wireOp",EDGE,"E14.2.11"),sQuery(id+"F0.wireOp",EDGE,"E15.2.3.0"),sQuery(id+"F0.wireOp",EDGE,"E15.4.3.0"),sQuery(id+"F0.wireOp",EDGE,"E15.7.3.0"),sQuery(id+"F0.wireOp",EDGE,"E15.11.3.0"),sQuery(id+"F0.wireOp",EDGE,"E15.15.3.0"),sQuery(id+"F0.wireOp",EDGE,"E15.19.3.0"),sQuery(id+"F0.wireOp",EDGE,"E15.22.3.0"),sQuery(id+"F0.wireOp",EDGE,"E15.25.3.0"),sQuery(id+"F0.wireOp",EDGE,"E15.29.3.0"),sQuery(id+"F0.wireOp",EDGE,"E15.33.3.0"),sQuery(id+"F0.wireOp",EDGE,"E15.37.3.0"),sQuery(id+"F0.wireOp",EDGE,"E15.40.3.0"),sQuery(id+"F0.wireOp",EDGE,"E15.2.4.0"),sQuery(id+"F0.wireOp",EDGE,"E15.4.4.0"),sQuery(id+"F0.wireOp",EDGE,"E15.7.4.0"),sQuery(id+"F0.wireOp",EDGE,"E15.11.4.0"),sQuery(id+"F0.wireOp",EDGE,"E15.15.4.0"),sQuery(id+"F0.wireOp",EDGE,"E15.19.4.0"),sQuery(id+"F0.wireOp",EDGE,"E15.22.4.0"),sQuery(id+"F0.wireOp",EDGE,"E15.25.4.0"),sQuery(id+"F0.wireOp",EDGE,"E15.29.4.0"),sQuery(id+"F0.wireOp",EDGE,"E15.33.4.0"),sQuery(id+"F0.wireOp",EDGE,"E15.37.4.0"),sQuery(id+"F0.wireOp",EDGE,"E15.40.4.0"),sQuery(id+"F0.wireOp",EDGE,"E15.2.5.0"),sQuery(id+"F0.wireOp",EDGE,"E15.4.5.0"),sQuery(id+"F0.wireOp",EDGE,"E15.7.5.0"),sQuery(id+"F0.wireOp",EDGE,"E15.11.5.0"),sQuery(id+"F0.wireOp",EDGE,"E15.15.5.0"),sQuery(id+"F0.wireOp",EDGE,"E15.19.5.0"),sQuery(id+"F0.wireOp",EDGE,"E15.22.5.0"),sQuery(id+"F0.wireOp",EDGE,"E15.25.5.0"),sQuery(id+"F0.wireOp",EDGE,"E15.29.5.0"),sQuery(id+"F0.wireOp",EDGE,"E15.33.5.0"),sQuery(id+"F0.wireOp",EDGE,"E15.37.5.0"),sQuery(id+"F0.wireOp",EDGE,"E15.40.5.0"),sQuery(id+"F0.wireOp",EDGE,"E15.2.6.0"),sQuery(id+"F0.wireOp",EDGE,"E15.4.6.0"),sQuery(id+"F0.wireOp",EDGE,"E15.7.6.0"),sQuery(id+"F0.wireOp",EDGE,"E15.11.6.0"),sQuery(id+"F0.wireOp",EDGE,"E15.15.6.0"),sQuery(id+"F0.wireOp",EDGE,"E15.19.6.0"),sQuery(id+"F0.wireOp",EDGE,"E15.22.6.0"),sQuery(id+"F0.wireOp",EDGE,"E15.25.6.0"),sQuery(id+"F0.wireOp",EDGE,"E15.29.6.0"),sQuery(id+"F0.wireOp",EDGE,"E15.33.6.0"),sQuery(id+"F0.wireOp",EDGE,"E15.37.6.0"),sQuery(id+"F0.wireOp",EDGE,"E15.40.6.0"),sQuery(id+"F0.wireOp",EDGE,"E15.2.7.0"),sQuery(id+"F0.wireOp",EDGE,"E15.4.7.0"),sQuery(id+"F0.wireOp",EDGE,"E15.7.7.0"),sQuery(id+"F0.wireOp",EDGE,"E15.11.7.0"),sQuery(id+"F0.wireOp",EDGE,"E15.15.7.0"),sQuery(id+"F0.wireOp",EDGE,"E15.19.7.0"),sQuery(id+"F0.wireOp",EDGE,"E15.22.7.0"),sQuery(id+"F0.wireOp",EDGE,"E15.25.7.0"),sQuery(id+"F0.wireOp",EDGE,"E15.29.7.0"),sQuery(id+"F0.wireOp",EDGE,"E15.33.7.0"),sQuery(id+"F0.wireOp",EDGE,"E15.37.7.0"),sQuery(id+"F0.wireOp",EDGE,"E15.40.7.0"),sQuery(id+"F0.wireOp",EDGE,"E15.2.8.0"),sQuery(id+"F0.wireOp",EDGE,"E15.4.8.0"),sQuery(id+"F0.wireOp",EDGE,"E15.7.8.0"),sQuery(id+"F0.wireOp",EDGE,"E15.11.8.0"),sQuery(id+"F0.wireOp",EDGE,"E15.15.8.0"),sQuery(id+"F0.wireOp",EDGE,"E15.19.8.0"),sQuery(id+"F0.wireOp",EDGE,"E15.22.8.0"),sQuery(id+"F0.wireOp",EDGE,"E15.25.8.0"),sQuery(id+"F0.wireOp",EDGE,"E15.29.8.0"),sQuery(id+"F0.wireOp",EDGE,"E15.33.8.0"),sQuery(id+"F0.wireOp",EDGE,"E15.37.8.0"),sQuery(id+"F0.wireOp",EDGE,"E15.40.8.0"),sQuery(id+"F0.wireOp",EDGE,"E15.2.9.0"),sQuery(id+"F0.wireOp",EDGE,"E15.4.9.0"),sQuery(id+"F0.wireOp",EDGE,"E15.7.9.0"),sQuery(id+"F0.wireOp",EDGE,"E15.11.9.0"),sQuery(id+"F0.wireOp",EDGE,"E15.15.9.0"),sQuery(id+"F0.wireOp",EDGE,"E15.19.9.0"),sQuery(id+"F0.wireOp",EDGE,"E15.22.9.0"),sQuery(id+"F0.wireOp",EDGE,"E15.25.9.0"),sQuery(id+"F0.wireOp",EDGE,"E15.29.9.0"),sQuery(id+"F0.wireOp",EDGE,"E15.33.9.0"),sQuery(id+"F0.wireOp",EDGE,"E15.37.9.0"),sQuery(id+"F0.wireOp",EDGE,"E15.40.9.0"),sQuery(id+"F0.wireOp",EDGE,"E15.2.10.0"),sQuery(id+"F0.wireOp",EDGE,"E15.4.10.0"),sQuery(id+"F0.wireOp",EDGE,"E15.7.10.0"),sQuery(id+"F0.wireOp",EDGE,"E15.11.10.0"),sQuery(id+"F0.wireOp",EDGE,"E15.15.10.0"),sQuery(id+"F0.wireOp",EDGE,"E15.19.10.0"),sQuery(id+"F0.wireOp",EDGE,"E15.22.10.0"),sQuery(id+"F0.wireOp",EDGE,"E15.25.10.0"),sQuery(id+"F0.wireOp",EDGE,"E15.29.10.0"),sQuery(id+"F0.wireOp",EDGE,"E15.33.10.0"),sQuery(id+"F0.wireOp",EDGE,"E15.37.10.0"),sQuery(id+"F0.wireOp",EDGE,"E15.40.10.0"),sQuery(id+"F0.wireOp",EDGE,"E15.2.11.0"),sQuery(id+"F0.wireOp",EDGE,"E15.4.11.0"),sQuery(id+"F0.wireOp",EDGE,"E15.7.11.0"),sQuery(id+"F0.wireOp",EDGE,"E15.11.11.0"),sQuery(id+"F0.wireOp",EDGE,"E15.15.11.0"),sQuery(id+"F0.wireOp",EDGE,"E15.19.11.0"),sQuery(id+"F0.wireOp",EDGE,"E15.22.11.0"),sQuery(id+"F0.wireOp",EDGE,"E15.25.11.0"),sQuery(id+"F0.wireOp",EDGE,"E15.29.11.0"),sQuery(id+"F0.wireOp",EDGE,"E15.33.11.0"),sQuery(id+"F0.wireOp",EDGE,"E15.37.11.0"),sQuery(id+"F0.wireOp",EDGE,"E15.40.11.0"),sQuery(id+"F0.wireOp",EDGE,"E15.2.12.0"),sQuery(id+"F0.wireOp",EDGE,"E15.4.12.0"),sQuery(id+"F0.wireOp",EDGE,"E15.7.12.0"),sQuery(id+"F0.wireOp",EDGE,"E15.11.12.0"),sQuery(id+"F0.wireOp",EDGE,"E15.15.12.0"),sQuery(id+"F0.wireOp",EDGE,"E15.19.12.0"),sQuery(id+"F0.wireOp",EDGE,"E15.22.12.0"),sQuery(id+"F0.wireOp",EDGE,"E15.25.12.0"),sQuery(id+"F0.wireOp",EDGE,"E15.29.12.0"),sQuery(id+"F0.wireOp",EDGE,"E15.33.12.0"),sQuery(id+"F0.wireOp",EDGE,"E15.37.12.0"),sQuery(id+"F0.wireOp",EDGE,"E15.40.12.0"),sQuery(id+"F0.wireOp",EDGE,"E15.2.13.0"),sQuery(id+"F0.wireOp",EDGE,"E15.4.13.0"),sQuery(id+"F0.wireOp",EDGE,"E15.7.13.0"),sQuery(id+"F0.wireOp",EDGE,"E15.11.13.0"),sQuery(id+"F0.wireOp",EDGE,"E15.15.13.0"),sQuery(id+"F0.wireOp",EDGE,"E15.19.13.0"),sQuery(id+"F0.wireOp",EDGE,"E15.22.13.0"),sQuery(id+"F0.wireOp",EDGE,"E15.25.13.0"),sQuery(id+"F0.wireOp",EDGE,"E15.29.13.0"),sQuery(id+"F0.wireOp",EDGE,"E15.33.13.0"),sQuery(id+"F0.wireOp",EDGE,"E15.37.13.0"),sQuery(id+"F0.wireOp",EDGE,"E15.40.13.0"),sQuery(id+"F0.wireOp",EDGE,"E15.2.14.0"),sQuery(id+"F0.wireOp",EDGE,"E15.4.14.0"),sQuery(id+"F0.wireOp",EDGE,"E15.7.14.0"),sQuery(id+"F0.wireOp",EDGE,"E15.11.14.0"),sQuery(id+"F0.wireOp",EDGE,"E15.15.14.0"),sQuery(id+"F0.wireOp",EDGE,"E15.19.14.0"),sQuery(id+"F0.wireOp",EDGE,"E15.22.14.0"),sQuery(id+"F0.wireOp",EDGE,"E15.25.14.0"),sQuery(id+"F0.wireOp",EDGE,"E15.29.14.0"),sQuery(id+"F0.wireOp",EDGE,"E15.33.14.0"),sQuery(id+"F0.wireOp",EDGE,"E15.37.14.0"),sQuery(id+"F0.wireOp",EDGE,"E15.40.14.0"),sQuery(id+"F0.wireOp",EDGE,"E15.2.15.0"),sQuery(id+"F0.wireOp",EDGE,"E15.4.15.0"),sQuery(id+"F0.wireOp",EDGE,"E15.7.15.0"),sQuery(id+"F0.wireOp",EDGE,"E15.11.15.0"),sQuery(id+"F0.wireOp",EDGE,"E15.15.15.0"),sQuery(id+"F0.wireOp",EDGE,"E15.19.15.0"),sQuery(id+"F0.wireOp",EDGE,"E15.22.15.0"),sQuery(id+"F0.wireOp",EDGE,"E15.25.15.0"),sQuery(id+"F0.wireOp",EDGE,"E15.29.15.0"),sQuery(id+"F0.wireOp",EDGE,"E15.33.15.0"),sQuery(id+"F0.wireOp",EDGE,"E15.37.15.0"),sQuery(id+"F0.wireOp",EDGE,"E15.40.15.0"),sQuery(id+"F0.wireOp",EDGE,"E15.2.16.0"),sQuery(id+"F0.wireOp",EDGE,"E15.4.16.0"),sQuery(id+"F0.wireOp",EDGE,"E15.7.16.0"),sQuery(id+"F0.wireOp",EDGE,"E15.11.16.0"),sQuery(id+"F0.wireOp",EDGE,"E15.15.16.0"),sQuery(id+"F0.wireOp",EDGE,"E15.19.16.0"),sQuery(id+"F0.wireOp",EDGE,"E15.22.16.0"),sQuery(id+"F0.wireOp",EDGE,"E15.25.16.0"),sQuery(id+"F0.wireOp",EDGE,"E15.29.16.0"),sQuery(id+"F0.wireOp",EDGE,"E15.33.16.0"),sQuery(id+"F0.wireOp",EDGE,"E15.37.16.0"),sQuery(id+"F0.wireOp",EDGE,"E15.40.16.0"),sQuery(id+"F0.wireOp",EDGE,"E15.2.17.0"),sQuery(id+"F0.wireOp",EDGE,"E15.4.17.0"),sQuery(id+"F0.wireOp",EDGE,"E15.7.17.0"),sQuery(id+"F0.wireOp",EDGE,"E15.11.17.0"),sQuery(id+"F0.wireOp",EDGE,"E15.15.17.0"),sQuery(id+"F0.wireOp",EDGE,"E15.19.17.0"),sQuery(id+"F0.wireOp",EDGE,"E15.22.17.0"),sQuery(id+"F0.wireOp",EDGE,"E15.25.17.0"),sQuery(id+"F0.wireOp",EDGE,"E15.29.17.0"),sQuery(id+"F0.wireOp",EDGE,"E15.33.17.0"),sQuery(id+"F0.wireOp",EDGE,"E15.37.17.0"),sQuery(id+"F0.wireOp",EDGE,"E15.40.17.0"),sQuery(id+"F0.wireOp",EDGE,"E15.2.18.0"),sQuery(id+"F0.wireOp",EDGE,"E15.4.18.0"),sQuery(id+"F0.wireOp",EDGE,"E15.7.18.0"),sQuery(id+"F0.wireOp",EDGE,"E15.11.18.0"),sQuery(id+"F0.wireOp",EDGE,"E15.15.18.0"),sQuery(id+"F0.wireOp",EDGE,"E15.19.18.0"),sQuery(id+"F0.wireOp",EDGE,"E15.22.18.0"),sQuery(id+"F0.wireOp",EDGE,"E15.25.18.0"),sQuery(id+"F0.wireOp",EDGE,"E15.29.18.0"),sQuery(id+"F0.wireOp",EDGE,"E15.33.18.0"),sQuery(id+"F0.wireOp",EDGE,"E15.37.18.0"),sQuery(id+"F0.wireOp",EDGE,"E15.40.18.0"),sQuery(id+"F0.wireOp",EDGE,"E15.2.19.0"),sQuery(id+"F0.wireOp",EDGE,"E15.4.19.0"),sQuery(id+"F0.wireOp",EDGE,"E15.7.19.0"),sQuery(id+"F0.wireOp",EDGE,"E15.11.19.0"),sQuery(id+"F0.wireOp",EDGE,"E15.15.19.0"),sQuery(id+"F0.wireOp",EDGE,"E15.19.19.0"),sQuery(id+"F0.wireOp",EDGE,"E15.22.19.0"),sQuery(id+"F0.wireOp",EDGE,"E15.25.19.0"),sQuery(id+"F0.wireOp",EDGE,"E15.29.19.0"),sQuery(id+"F0.wireOp",EDGE,"E15.33.19.0"),sQuery(id+"F0.wireOp",EDGE,"E15.37.19.0"),sQuery(id+"F0.wireOp",EDGE,"E15.40.19.0"),sQuery(id+"F0.wireOp",EDGE,"E15.2.20.0"),sQuery(id+"F0.wireOp",EDGE,"E15.4.20.0"),sQuery(id+"F0.wireOp",EDGE,"E15.7.20.0"),sQuery(id+"F0.wireOp",EDGE,"E15.11.20.0"),sQuery(id+"F0.wireOp",EDGE,"E15.15.20.0"),sQuery(id+"F0.wireOp",EDGE,"E15.19.20.0"),sQuery(id+"F0.wireOp",EDGE,"E15.22.20.0"),sQuery(id+"F0.wireOp",EDGE,"E15.25.20.0"),sQuery(id+"F0.wireOp",EDGE,"E15.29.20.0"),sQuery(id+"F0.wireOp",EDGE,"E15.33.20.0"),sQuery(id+"F0.wireOp",EDGE,"E15.37.20.0"),sQuery(id+"F0.wireOp",EDGE,"E15.40.20.0"),sQuery(id+"F0.wireOp",EDGE,"E15.2.21.0"),sQuery(id+"F0.wireOp",EDGE,"E15.4.21.0"),sQuery(id+"F0.wireOp",EDGE,"E15.7.21.0"),sQuery(id+"F0.wireOp",EDGE,"E15.11.21.0"),sQuery(id+"F0.wireOp",EDGE,"E15.15.21.0"),sQuery(id+"F0.wireOp",EDGE,"E15.19.21.0"),sQuery(id+"F0.wireOp",EDGE,"E15.22.21.0"),sQuery(id+"F0.wireOp",EDGE,"E15.25.21.0"),sQuery(id+"F0.wireOp",EDGE,"E15.29.21.0"),sQuery(id+"F0.wireOp",EDGE,"E15.33.21.0"),sQuery(id+"F0.wireOp",EDGE,"E15.37.21.0"),sQuery(id+"F0.wireOp",EDGE,"E15.40.21.0"),sQuery(id+"F0.wireOp",EDGE,"E15.2.22.0"),sQuery(id+"F0.wireOp",EDGE,"E15.4.22.0"),sQuery(id+"F0.wireOp",EDGE,"E15.7.22.0"),sQuery(id+"F0.wireOp",EDGE,"E15.11.22.0"),sQuery(id+"F0.wireOp",EDGE,"E15.15.22.0"),sQuery(id+"F0.wireOp",EDGE,"E15.19.22.0"),sQuery(id+"F0.wireOp",EDGE,"E15.22.22.0"),sQuery(id+"F0.wireOp",EDGE,"E15.25.22.0"),sQuery(id+"F0.wireOp",EDGE,"E15.29.22.0"),sQuery(id+"F0.wireOp",EDGE,"E15.33.22.0"),sQuery(id+"F0.wireOp",EDGE,"E15.37.22.0"),sQuery(id+"F0.wireOp",EDGE,"E15.40.22.0"),sQuery(id+"F0.wireOp",EDGE,"E15.2.23.0"),sQuery(id+"F0.wireOp",EDGE,"E15.4.23.0"),sQuery(id+"F0.wireOp",EDGE,"E15.7.23.0"),sQuery(id+"F0.wireOp",EDGE,"E15.11.23.0"),sQuery(id+"F0.wireOp",EDGE,"E15.15.23.0"),sQuery(id+"F0.wireOp",EDGE,"E15.19.23.0"),sQuery(id+"F0.wireOp",EDGE,"E15.22.23.0"),sQuery(id+"F0.wireOp",EDGE,"E15.25.23.0"),sQuery(id+"F0.wireOp",EDGE,"E15.29.23.0"),sQuery(id+"F0.wireOp",EDGE,"E15.33.23.0"),sQuery(id+"F0.wireOp",EDGE,"E15.37.23.0"),sQuery(id+"F0.wireOp",EDGE,"E15.40.23.0"),sQuery(id+"F0.wireOp",EDGE,"E16.trimOffspring"),sQuery(id+"F0.wireOp",EDGE,"E17.trimOffspring"),sQuery(id+"F0.wireOp",EDGE,"E18.trimOffspring"),sQuery(id+"F0.wireOp",EDGE,"E19.trimOffspring"),sQuery(id+"F0.wireOp",EDGE,"E20.trimOffspring"),sQuery(id+"F0.wireOp",EDGE,"E21.trimOffspring"),sQuery(id+"F0.wireOp",EDGE,"E22.trimOffspring"),sQuery(id+"F0.wireOp",EDGE,"E23.trimOffspring"),sQuery(id+"F0.wireOp",EDGE,"E24.trimOffspring"),sQuery(id+"F0.wireOp",EDGE,"E25.trimOffspring"),sQuery(id+"F0.wireOp",EDGE,"E26.trimOffspring"),sQuery(id+"F0.wireOp",EDGE,"E27.trimOffspring"),sQuery(id+"F0.wireOp",EDGE,"E28.trimOffspring"),sQuery(id+"F0.wireOp",EDGE,"E29.trimOffspring"),sQuery(id+"F0.wireOp",EDGE,"E30.trimOffspring"),sQuery(id+"F0.wireOp",EDGE,"E31.trimOffspring"),sQuery(id+"F0.wireOp",EDGE,"E32.trimOffspring"),sQuery(id+"F0.wireOp",EDGE,"E33.trimOffspring"),sQuery(id+"F0.wireOp",EDGE,"E34.trimOffspring"),sQuery(id+"F0.wireOp",EDGE,"E35.trimOffspring"),sQuery(id+"F0.wireOp",EDGE,"E36.trimOffspring"),sQuery(id+"F0.wireOp",EDGE,"E37.trimOffspring"),sQuery(id+"F0.wireOp",EDGE,"E38.trimOffspring")])],"isStart":true});
            var sketch = newSketch(context, id + "F4", { "sketchPlane" : qUnion([Q0])});
            skCircle(sketch, "E40", {"center": v(0, 0) * mm, "radius": 3.18 * mm});
            skSolve(sketch);
        }
        {
            var Q0;
            Q0 = qSketchRegion(id + "F4", true);
            extrude(context, id + "F5", {"entities" : qUnion([Q0]), "operationType" : NewBodyOperationType.REMOVE, "oppositeDirection" : true, "depth" : 5.08 * mm});
        }
    });
